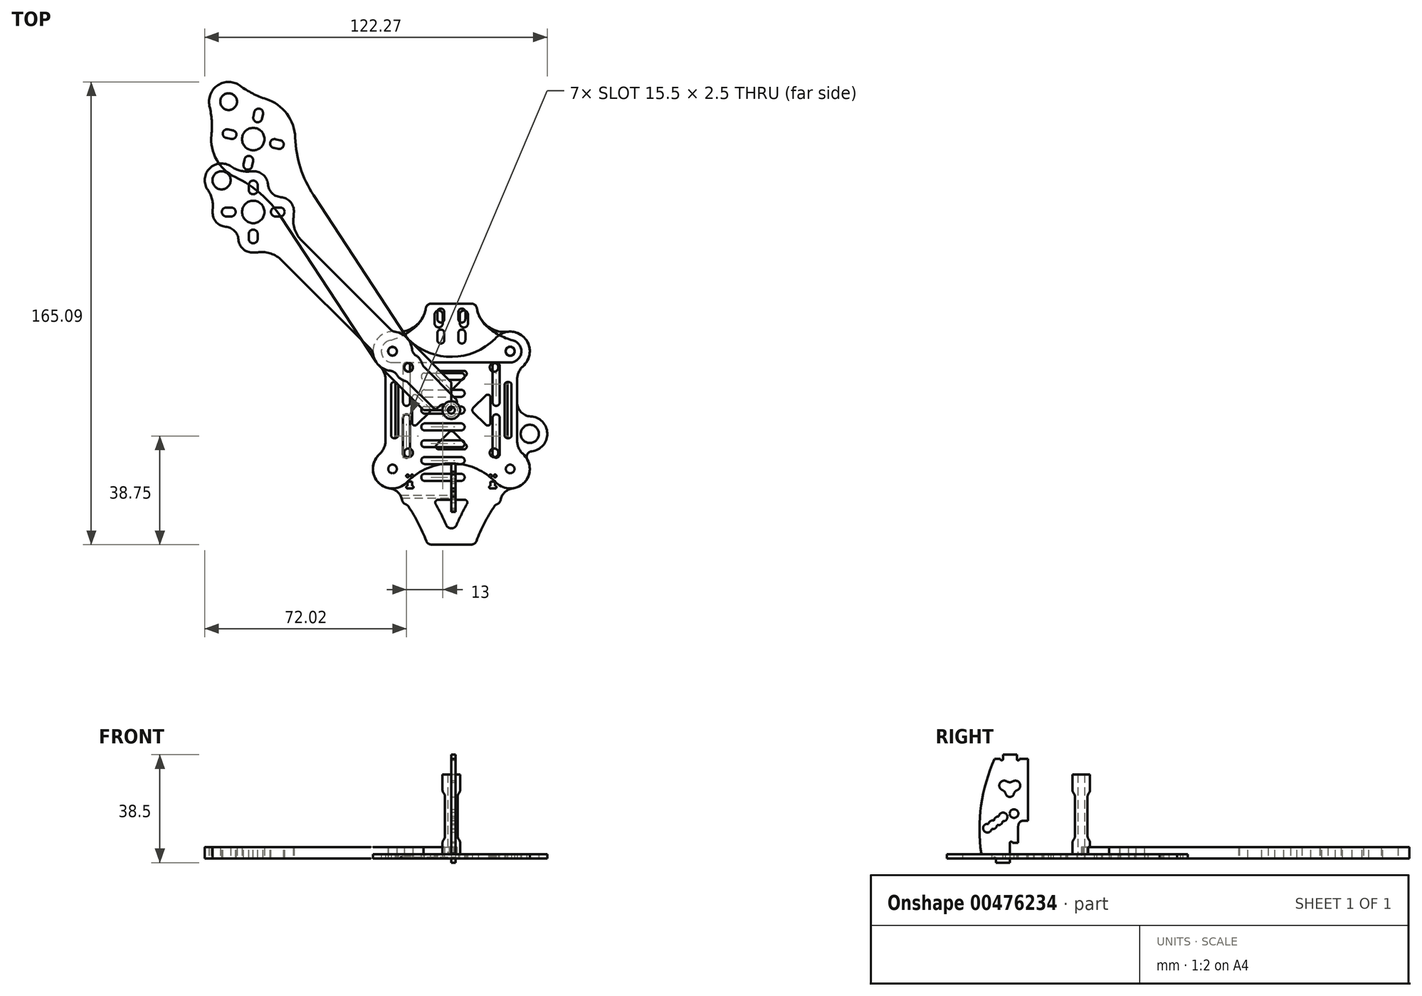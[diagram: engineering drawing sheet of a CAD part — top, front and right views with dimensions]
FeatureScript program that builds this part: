
annotation { "Feature Type Name" : "Feature", "Feature Type Description" : "" }
export const myFeature = defineFeature(function(context is Context, id is Id, definition is map)
    precondition{}
    {
        {
            var Q0;
            Q0=qCreatedBy(makeId("Top.planeOp"),FACE);
            var sketch = newSketch(context, id + "F0", { "sketchPlane" : qUnion([Q0])});
            skCircle(sketch, "E0", {"center": v(-15.25, 15.25) * mm, "radius": 1.55 * mm});
            skCircle(sketch, "E1", {"center": v(15.25, 15.25) * mm, "radius": 1.55 * mm});
            skCircle(sketch, "E2", {"center": v(15.25, -15.25) * mm, "radius": 1.55 * mm});
            skCircle(sketch, "E3", {"center": v(-15.25, -15.25) * mm, "radius": 1.55 * mm});
            skCircle(sketch, "E4", {"center": v(-21, 21) * mm, "radius": 1.55 * mm});
            skCircle(sketch, "E5.MirrorC", {"center": v(21, 21) * mm, "radius": 1.55 * mm});
            skCircle(sketch, "E6.MirrorC", {"center": v(-21, -21) * mm, "radius": 1.55 * mm});
            skCircle(sketch, "E7.MirrorC", {"center": v(21, -21) * mm, "radius": 1.55 * mm});
            skArc(sketch, "E8", {"start": v(-16.05, 25.95) * mm, "mid": v(-25.95, 25.95) * mm, "end": v(-25.95, 16.05) * mm});
            skLineSegment(sketch, "E9", {"start": v(-19, 9) * mm, "end": v(-19, -9) * mm});
            skLineSegment(sketch, "E10", {"start": v(-16.05, 25.95) * mm, "end": v(-15.56, 25.46) * mm});
            skLineSegment(sketch, "E11", {"start": v(-25.95, 16.05) * mm, "end": v(-23.5, 13.6) * mm});
            skLineSegment(sketch, "E12.MirrorCS", {"start": v(-25.95, -16.05) * mm, "end": v(-23.5, -13.6) * mm});
            skArc(sketch, "E13.MirrorCS", {"start": v(-16.05, -25.95) * mm, "mid": v(-25.95, -25.95) * mm, "end": v(-25.95, -16.05) * mm});
            skLineSegment(sketch, "E14.MirrorCS", {"start": v(-16.05, -25.95) * mm, "end": v(-15.56, -25.46) * mm});
            skLineSegment(sketch, "E15.MirrorCS", {"start": v(16.05, 25.95) * mm, "end": v(15.56, 25.46) * mm});
            skArc(sketch, "E16.MirrorCS", {"start": v(16.05, 25.95) * mm, "mid": v(25.95, 25.95) * mm, "end": v(25.95, 16.05) * mm});
            skLineSegment(sketch, "E17.MirrorCS", {"start": v(25.95, 16.05) * mm, "end": v(23.5, 13.6) * mm});
            skLineSegment(sketch, "E18.MirrorCS", {"start": v(25.95, -16.05) * mm, "end": v(23.5, -13.6) * mm});
            skArc(sketch, "E19.MirrorCS", {"start": v(16.05, -25.95) * mm, "mid": v(25.95, -25.95) * mm, "end": v(25.95, -16.05) * mm});
            skLineSegment(sketch, "E20.MirrorCS", {"start": v(16.05, -25.95) * mm, "end": v(15.56, -25.46) * mm});
            skPoint(sketch, "E21.visualSharp", {"position": v(0, 9.9) * mm});
            skPoint(sketch, "E22.visualSharp", {"position": v(0, -9.9) * mm});
            skArc(sketch, "E22.filletArc", {"start": v(15.56, -25.46) * mm, "mid": v(0, -19.01) * mm, "end": v(-15.56, -25.46) * mm});
            skLineSegment(sketch, "E23", {"start": v(-21, 21) * mm, "end": v(0, 0) * mm, "construction": true});
            skArc(sketch, "E24.filletArc", {"start": v(-15.56, 25.46) * mm, "mid": v(0, 19.01) * mm, "end": v(15.56, 25.46) * mm});
            skLineSegment(sketch, "E25", {"start": v(-21.5, 9) * mm, "end": v(-21.5, -9) * mm});
            skLineSegment(sketch, "E26", {"start": v(-23.5, 13.6) * mm, "end": v(-23.5, -13.6) * mm});
            skLineSegment(sketch, "E27", {"start": v(-20.5, 10) * mm, "end": v(-20, 10) * mm});
            skLineSegment(sketch, "E28", {"start": v(-20.5, -10) * mm, "end": v(-20, -10) * mm});
            skPoint(sketch, "E29.visualSharp", {"position": v(-21.5, 10) * mm});
            skArc(sketch, "E29.filletArc", {"start": v(-20.5, 10) * mm, "mid": v(-21.2, 9.7) * mm, "end": v(-21.5, 9) * mm});
            skPoint(sketch, "E30.visualSharp", {"position": v(-19, 10) * mm});
            skArc(sketch, "E30.filletArc", {"start": v(-19, 9) * mm, "mid": v(-19.3, 9.7) * mm, "end": v(-20, 10) * mm});
            skPoint(sketch, "E31.visualSharp", {"position": v(-21.5, -10) * mm});
            skArc(sketch, "E31.filletArc", {"start": v(-21.5, -9) * mm, "mid": v(-21.2, -9.7) * mm, "end": v(-20.5, -10) * mm});
            skPoint(sketch, "E32.visualSharp", {"position": v(-19, -10) * mm});
            skArc(sketch, "E32.filletArc", {"start": v(-20, -10) * mm, "mid": v(-19.3, -9.7) * mm, "end": v(-19, -9) * mm});
            skLineSegment(sketch, "E33.MirrorCS", {"start": v(20.5, -10) * mm, "end": v(20, -10) * mm});
            skLineSegment(sketch, "E34.MirrorCS", {"start": v(20.5, 10) * mm, "end": v(20, 10) * mm});
            skArc(sketch, "E35.MirrorCS", {"start": v(20, -10) * mm, "mid": v(19.3, -9.7) * mm, "end": v(19, -9) * mm});
            skArc(sketch, "E36.MirrorCS", {"start": v(20.5, 10) * mm, "mid": v(21.2, 9.7) * mm, "end": v(21.5, 9) * mm});
            skArc(sketch, "E37.MirrorCS", {"start": v(21.5, -9) * mm, "mid": v(21.2, -9.7) * mm, "end": v(20.5, -10) * mm});
            skArc(sketch, "E38.MirrorCS", {"start": v(19, 9) * mm, "mid": v(19.3, 9.7) * mm, "end": v(20, 10) * mm});
            skPoint(sketch, "E39.MirrorP", {"position": v(19, -10) * mm});
            skLineSegment(sketch, "E40.MirrorCS", {"start": v(23.5, 13.6) * mm, "end": v(23.5, -13.6) * mm});
            skLineSegment(sketch, "E41.MirrorCS", {"start": v(19, 9) * mm, "end": v(19, -9) * mm});
            skPoint(sketch, "E42.MirrorP", {"position": v(21.5, -10) * mm});
            skPoint(sketch, "E43.MirrorP", {"position": v(21.5, 10) * mm});
            skPoint(sketch, "E44.MirrorP", {"position": v(19, 10) * mm});
            skLineSegment(sketch, "E45.MirrorCS", {"start": v(21.5, 9) * mm, "end": v(21.5, -9) * mm});
            skLineSegment(sketch, "E46", {"start": v(0, 0) * mm, "end": v(21, -21) * mm, "construction": true});
            skLineSegment(sketch, "E47", {"start": v(21, 21) * mm, "end": v(-21, -21) * mm, "construction": true});
            skLineSegment(sketch, "E48.0", {"start": v(0.7, -7.78) * mm, "end": v(5.22, -12.3) * mm});
            skLineSegment(sketch, "E48.1", {"start": v(-12.3, 5.22) * mm, "end": v(-7.78, 0.7) * mm});
            skLineSegment(sketch, "E49.0", {"start": v(-5.22, 12.3) * mm, "end": v(-0.7, 7.78) * mm});
            skLineSegment(sketch, "E50.0", {"start": v(7.78, -0.7) * mm, "end": v(12.3, -5.22) * mm});
            skLineSegment(sketch, "E51.MirrorCS", {"start": v(5.22, 12.3) * mm, "end": v(0.7, 7.78) * mm});
            skLineSegment(sketch, "E52.MirrorCS", {"start": v(12.3, 5.22) * mm, "end": v(7.78, 0.7) * mm});
            skLineSegment(sketch, "E53.MirrorCS", {"start": v(-0.7, -7.78) * mm, "end": v(-5.22, -12.3) * mm});
            skLineSegment(sketch, "E54.MirrorCS", {"start": v(-7.78, -0.7) * mm, "end": v(-12.3, -5.22) * mm});
            skPoint(sketch, "E55.orphan", {"position": v(-3.54, -3.54) * mm});
            skPoint(sketch, "E56.orphan", {"position": v(3.54, -3.54) * mm});
            skLineSegment(sketch, "E57", {"start": v(-4.51, 14) * mm, "end": v(4.51, 14) * mm});
            skLineSegment(sketch, "E58", {"start": v(-14, 4.51) * mm, "end": v(-14, -4.51) * mm});
            skLineSegment(sketch, "E59", {"start": v(-4.51, -14) * mm, "end": v(4.51, -14) * mm});
            skLineSegment(sketch, "E60", {"start": v(14, -4.51) * mm, "end": v(14, 4.51) * mm});
            skPoint(sketch, "E61.visualSharp", {"position": v(-14, 6.93) * mm});
            skArc(sketch, "E61.filletArc", {"start": v(-12.3, 5.22) * mm, "mid": v(-13.38, 5.44) * mm, "end": v(-14, 4.51) * mm});
            skPoint(sketch, "E62.visualSharp", {"position": v(-14, -6.93) * mm});
            skArc(sketch, "E62.filletArc", {"start": v(-14, -4.51) * mm, "mid": v(-13.38, -5.44) * mm, "end": v(-12.3, -5.22) * mm});
            skPoint(sketch, "E63.visualSharp", {"position": v(-7.07, 0) * mm});
            skArc(sketch, "E63.filletArc", {"start": v(-7.78, -0.7) * mm, "mid": v(-7.49, 0) * mm, "end": v(-7.78, 0.7) * mm});
            skPoint(sketch, "E64.visualSharp", {"position": v(0, -7.07) * mm});
            skArc(sketch, "E64.filletArc", {"start": v(0.7, -7.78) * mm, "mid": v(0, -7.49) * mm, "end": v(-0.7, -7.78) * mm});
            skPoint(sketch, "E65.visualSharp", {"position": v(-6.93, -14) * mm});
            skArc(sketch, "E65.filletArc", {"start": v(-5.22, -12.3) * mm, "mid": v(-5.44, -13.38) * mm, "end": v(-4.51, -14) * mm});
            skPoint(sketch, "E66.visualSharp", {"position": v(6.93, -14) * mm});
            skArc(sketch, "E66.filletArc", {"start": v(4.51, -14) * mm, "mid": v(5.44, -13.38) * mm, "end": v(5.22, -12.3) * mm});
            skPoint(sketch, "E67.visualSharp", {"position": v(14, -6.93) * mm});
            skArc(sketch, "E67.filletArc", {"start": v(12.3, -5.22) * mm, "mid": v(13.38, -5.44) * mm, "end": v(14, -4.51) * mm});
            skPoint(sketch, "E68.visualSharp", {"position": v(14, 6.93) * mm});
            skArc(sketch, "E68.filletArc", {"start": v(14, 4.51) * mm, "mid": v(13.38, 5.44) * mm, "end": v(12.3, 5.22) * mm});
            skPoint(sketch, "E69.visualSharp", {"position": v(7.07, 0) * mm});
            skArc(sketch, "E69.filletArc", {"start": v(7.78, 0.7) * mm, "mid": v(7.49, 0) * mm, "end": v(7.78, -0.7) * mm});
            skPoint(sketch, "E70.visualSharp", {"position": v(0, 7.07) * mm});
            skArc(sketch, "E70.filletArc", {"start": v(-0.7, 7.78) * mm, "mid": v(0, 7.49) * mm, "end": v(0.7, 7.78) * mm});
            skPoint(sketch, "E71.visualSharp", {"position": v(-6.93, 14) * mm});
            skArc(sketch, "E71.filletArc", {"start": v(-4.51, 14) * mm, "mid": v(-5.44, 13.38) * mm, "end": v(-5.22, 12.3) * mm});
            skPoint(sketch, "E72.visualSharp", {"position": v(6.93, 14) * mm});
            skArc(sketch, "E72.filletArc", {"start": v(5.22, 12.3) * mm, "mid": v(5.44, 13.38) * mm, "end": v(4.51, 14) * mm});
            skSolve(sketch);
        }
        {
            var Q0;
            Q0=makeQuery(id+"F0.imprint","IMPRINT",FACE,{"disambiguationData":[TD([[makeQuery(id+"F0.imprint","IMPRINT",EDGE,{"derivedFrom":sQuery(id+"F0.wireOp",EDGE,"E0")}),-1.0]])]});
            extrude(context, id + "F1", {"entities" : qUnion([Q0]), "depth" : 1.5 * mm});
        }
        {
            var Q0;
            Q0=qCreatedBy(makeId("Top.planeOp"),FACE);
            var sketch = newSketch(context, id + "F2", { "sketchPlane" : qUnion([Q0])});
            skCircle(sketch, "E73", {"center": v(-15.25, 15.25) * mm, "radius": 1.55 * mm});
            skCircle(sketch, "E74", {"center": v(-21, 21) * mm, "radius": 1.55 * mm});
            skArc(sketch, "E75", {"start": v(-20.18, 27.95) * mm, "mid": v(-27.3, 24.06) * mm, "end": v(-25.95, 16.05) * mm});
            skLineSegment(sketch, "E76", {"start": v(-19, 9) * mm, "end": v(-19, 0) * mm});
            skPoint(sketch, "E77.visualSharp", {"position": v(-19, 10) * mm});
            skArc(sketch, "E77.filletArc", {"start": v(-19, 9) * mm, "mid": v(-19.26, 9.67) * mm, "end": v(-19.9, 10) * mm});
            skLineSegment(sketch, "E78", {"start": v(0, 38) * mm, "end": v(0, -38) * mm, "construction": true});
            skArc(sketch, "E79.MirrorCS", {"start": v(19, 9) * mm, "mid": v(19.26, 9.67) * mm, "end": v(19.9, 10) * mm});
            skLineSegment(sketch, "E80.MirrorCS", {"start": v(19, 9) * mm, "end": v(19, 0) * mm});
            skArc(sketch, "E81.MirrorCS", {"start": v(20.18, 27.95) * mm, "mid": v(27.3, 24.06) * mm, "end": v(25.95, 16.05) * mm});
            skCircle(sketch, "E82.MirrorC", {"center": v(21, 21) * mm, "radius": 1.55 * mm});
            skCircle(sketch, "E83.MirrorC", {"center": v(15.25, 15.25) * mm, "radius": 1.55 * mm});
            skPoint(sketch, "E84.MirrorP", {"position": v(19, 10) * mm});
            skPoint(sketch, "E85.MirrorP", {"position": v(19, -10) * mm});
            skArc(sketch, "E86.MirrorCS", {"start": v(19, -9) * mm, "mid": v(19.26, -9.67) * mm, "end": v(19.9, -10) * mm});
            skLineSegment(sketch, "E87.MirrorCS", {"start": v(19, -9) * mm, "end": v(19, 0) * mm});
            skArc(sketch, "E88.MirrorCS", {"start": v(-19, -9) * mm, "mid": v(-19.26, -9.67) * mm, "end": v(-19.9, -10) * mm});
            skLineSegment(sketch, "E89.MirrorCS", {"start": v(-19, -9) * mm, "end": v(-19, 0) * mm});
            skPoint(sketch, "E90.MirrorP", {"position": v(-19, -10) * mm});
            skCircle(sketch, "E91.MirrorC", {"center": v(-15.25, -15.25) * mm, "radius": 1.55 * mm});
            skCircle(sketch, "E92.MirrorC", {"center": v(-21, -21) * mm, "radius": 1.55 * mm});
            skArc(sketch, "E93.MirrorCS", {"start": v(-22.14, -27.9) * mm, "mid": v(-27.66, -23.14) * mm, "end": v(-25.95, -16.05) * mm});
            skCircle(sketch, "E94.MirrorC", {"center": v(21, -21) * mm, "radius": 1.55 * mm});
            skCircle(sketch, "E95.MirrorC", {"center": v(15.25, -15.25) * mm, "radius": 1.55 * mm});
            skArc(sketch, "E96.MirrorCS", {"start": v(22.14, -27.9) * mm, "mid": v(27.66, -23.14) * mm, "end": v(25.95, -16.05) * mm});
            skArc(sketch, "E97.MirrorCS", {"start": v(22.14, -27.9) * mm, "mid": v(21.69, -28) * mm, "end": v(21.24, -28.1) * mm});
            skArc(sketch, "E98.MirrorCS", {"start": v(-22.14, -27.9) * mm, "mid": v(-21.69, -28) * mm, "end": v(-21.24, -28.1) * mm});
            skLineSegment(sketch, "E99.bottom", {"start": v(-15.6, -25.5) * mm, "end": v(-14, -25.5) * mm});
            skLineSegment(sketch, "E99.top", {"start": v(-15.6, -30.5) * mm, "end": v(-14, -30.5) * mm});
            skLineSegment(sketch, "E99.left", {"start": v(-15.6, -25.5) * mm, "end": v(-15.6, -30.5) * mm});
            skLineSegment(sketch, "E99.right", {"start": v(-14, -25.5) * mm, "end": v(-14, -30.5) * mm});
            skLineSegment(sketch, "E100.MirrorCS", {"start": v(15.6, -25.5) * mm, "end": v(14, -25.5) * mm});
            skLineSegment(sketch, "E101.MirrorCS", {"start": v(15.6, -25.5) * mm, "end": v(15.6, -30.5) * mm});
            skLineSegment(sketch, "E102.MirrorCS", {"start": v(14, -25.5) * mm, "end": v(14, -30.5) * mm});
            skLineSegment(sketch, "E103.MirrorCS", {"start": v(15.6, -30.5) * mm, "end": v(14, -30.5) * mm});
            skLineSegment(sketch, "E104", {"start": v(-25.95, -16.05) * mm, "end": v(-25.95, -16.05) * mm});
            skLineSegment(sketch, "E105", {"start": v(-21, -21) * mm, "end": v(0, 0) * mm, "construction": true});
            skLineSegment(sketch, "E106", {"start": v(-17.5, -32.94) * mm, "end": v(-17.5, -33.5) * mm});
            skLineSegment(sketch, "E107", {"start": v(-17.5, -33.5) * mm, "end": v(-16.97, -33.5) * mm});
            skLineSegment(sketch, "E108.MirrorCS", {"start": v(17.5, -32.94) * mm, "end": v(17.5, -33.5) * mm});
            skLineSegment(sketch, "E109.MirrorCS", {"start": v(17.5, -33.5) * mm, "end": v(16.97, -33.5) * mm});
            skArc(sketch, "E110.filletArc", {"start": v(-17.5, -32.94) * mm, "mid": v(-18.54, -29.88) * mm, "end": v(-21.24, -28.1) * mm});
            skArc(sketch, "E111.filletArc", {"start": v(21.24, -28.1) * mm, "mid": v(18.54, -29.88) * mm, "end": v(17.5, -32.94) * mm});
            skLineSegment(sketch, "E112", {"start": v(-25.95, 16.05) * mm, "end": v(-19.9, 10) * mm});
            skLineSegment(sketch, "E113", {"start": v(0, 0) * mm, "end": v(-15.25, 15.25) * mm, "construction": true});
            skLineSegment(sketch, "E114.MirrorCS", {"start": v(-25.95, -16.05) * mm, "end": v(-19.9, -10) * mm});
            skLineSegment(sketch, "E115.MirrorCS", {"start": v(25.95, 16.05) * mm, "end": v(19.9, 10) * mm});
            skLineSegment(sketch, "E116.MirrorCS", {"start": v(25.95, -16.05) * mm, "end": v(19.9, -10) * mm});
            skLineSegment(sketch, "E117", {"start": v(-21, -21) * mm, "end": v(-70.71, -70.71) * mm, "construction": true});
            skCircle(sketch, "E118", {"center": v(-70.71, -70.71) * mm, "radius": 64.25 * mm, "construction": true});
            skArc(sketch, "E119", {"start": v(-8.47, -48) * mm, "mid": v(-11.5, -41) * mm, "end": v(-15.3, -34.4) * mm});
            skLineSegment(sketch, "E120", {"start": v(-8.47, -48) * mm, "end": v(0, -48) * mm});
            skArc(sketch, "E121.MirrorCS", {"start": v(8.47, -48) * mm, "mid": v(11.5, -41) * mm, "end": v(15.3, -34.4) * mm});
            skLineSegment(sketch, "E122.MirrorCS", {"start": v(8.47, -48) * mm, "end": v(0, -48) * mm});
            skArc(sketch, "E123", {"start": v(-20.18, 27.95) * mm, "mid": v(-12.97, 29.9) * mm, "end": v(-9.12, 36.31) * mm});
            skArc(sketch, "E124.MirrorCS", {"start": v(20.18, 27.95) * mm, "mid": v(12.97, 29.9) * mm, "end": v(9.12, 36.31) * mm});
            skPoint(sketch, "E125.visualSharp", {"position": v(-15.9, -33.5) * mm});
            skArc(sketch, "E125.filletArc", {"start": v(-15.3, -34.4) * mm, "mid": v(-16.02, -33.74) * mm, "end": v(-16.97, -33.5) * mm});
            skPoint(sketch, "E126.visualSharp", {"position": v(15.9, -33.5) * mm});
            skArc(sketch, "E126.filletArc", {"start": v(16.97, -33.5) * mm, "mid": v(16.02, -33.74) * mm, "end": v(15.3, -34.4) * mm});
            skLineSegment(sketch, "E127", {"start": v(-7.15, 38) * mm, "end": v(7.15, 38) * mm});
            skPoint(sketch, "E128.orphan", {"position": v(-8.47, 48) * mm});
            skPoint(sketch, "E129.orphan", {"position": v(8.47, 48) * mm});
            skPoint(sketch, "E130.visualSharp", {"position": v(-9, 38) * mm});
            skArc(sketch, "E130.filletArc", {"start": v(-7.15, 38) * mm, "mid": v(-8.45, 37.52) * mm, "end": v(-9.12, 36.31) * mm});
            skPoint(sketch, "E131.visualSharp", {"position": v(9, 38) * mm});
            skArc(sketch, "E131.filletArc", {"start": v(9.12, 36.31) * mm, "mid": v(8.45, 37.52) * mm, "end": v(7.15, 38) * mm});
            skCircle(sketch, "E132", {"center": v(0, 0) * mm, "radius": 5 * mm});
            skSolve(sketch);
        }
        {
            var Q0;
            Q0=makeQuery(id+"F2.imprint","IMPRINT",FACE,{"disambiguationData":[TD([[makeQuery(id+"F2.imprint","IMPRINT",EDGE,{"derivedFrom":sQuery(id+"F2.wireOp",EDGE,"E73")}),-1.0]])]});
            extrude(context, id + "F3", {"entities" : qUnion([Q0]), "depth" : 1.5 * mm});
        }
        {
            var Q0;
            Q0=makeQuery(id+"F3.opExtrude","CAP_FACE",FACE,{"disambiguationData":[OSD([sQuery(id+"F2.wireOp",EDGE,"E73"),sQuery(id+"F2.wireOp",EDGE,"jFPTTxz4-jLXj-DDCv-FC09-USVAbM95QFUD"),sQuery(id+"F2.wireOp",EDGE,"E74"),sQuery(id+"F2.wireOp",EDGE,"E75"),sQuery(id+"F2.wireOp",EDGE,"E76"),sQuery(id+"F2.wireOp",EDGE,"OV2Wl9yg-sUyD-2Hj2-rkXj-MTIEYF9VZsJK"),sQuery(id+"F2.wireOp",EDGE,"91e39d24-f0d0-409c-99ef-685c742f9300.filletArc"),sQuery(id+"F2.wireOp",EDGE,"E77.filletArc"),sQuery(id+"F2.wireOp",EDGE,"2RSG9yHZ-WQqx-c2xK-pqDh-UdEIjaxC7IlA"),sQuery(id+"F2.wireOp",EDGE,"4rgxPuH5-7xbP-ZsFa-2w6e-7YXQlRziYjOP"),sQuery(id+"F2.wireOp",EDGE,"aAb2sQRX-3QeW-SLoE-m21K-AacbavdIfjy6"),sQuery(id+"F2.wireOp",EDGE,"7c283ec5-88dc-4330-9acd-45fa73696fd10.MirrorCS"),sQuery(id+"F2.wireOp",EDGE,"E79.MirrorCS"),sQuery(id+"F2.wireOp",EDGE,"E80.MirrorCS"),sQuery(id+"F2.wireOp",EDGE,"E81.MirrorCS"),sQuery(id+"F2.wireOp",EDGE,"E82.MirrorC"),sQuery(id+"F2.wireOp",EDGE,"E792.MirrorC"),sQuery(id+"F2.wireOp",EDGE,"E83.MirrorC"),sQuery(id+"F2.wireOp",EDGE,"E794.MirrorCS"),sQuery(id+"F2.wireOp",EDGE,"E796.MirrorCS"),sQuery(id+"F2.wireOp",EDGE,"77becaeb-8b8b-4dc1-b250-45090536f0a20.MirrorCS"),sQuery(id+"F2.wireOp",EDGE,"26ce58a3-4cb5-4f15-a1e7-5b8d20efb5c40.MirrorCS"),sQuery(id+"F2.wireOp",EDGE,"E86.MirrorCS"),sQuery(id+"F2.wireOp",EDGE,"9822711c-84ae-4c2d-bbd4-b3a60979fe174.MirrorCS"),sQuery(id+"F2.wireOp",EDGE,"E87.MirrorCS"),sQuery(id+"F2.wireOp",EDGE,"9822711c-84ae-4c2d-bbd4-b3a60979fe176.MirrorCS"),sQuery(id+"F2.wireOp",EDGE,"E88.MirrorCS"),sQuery(id+"F2.wireOp",EDGE,"4a2114cf-ddcc-4bd1-b273-f588f7a722dc1.MirrorCS"),sQuery(id+"F2.wireOp",EDGE,"4a2114cf-ddcc-4bd1-b273-f588f7a722dc2.MirrorCS"),sQuery(id+"F2.wireOp",EDGE,"E89.MirrorCS"),sQuery(id+"F2.wireOp",EDGE,"E91.MirrorC"),sQuery(id+"F2.wireOp",EDGE,"E92.MirrorC"),sQuery(id+"F2.wireOp",EDGE,"E93.MirrorCS"),sQuery(id+"F2.wireOp",EDGE,"E94.MirrorC"),sQuery(id+"F2.wireOp",EDGE,"E95.MirrorC"),sQuery(id+"F2.wireOp",EDGE,"5bfa031d-9f72-4db7-bc0c-70e661b370ed0.MirrorC"),sQuery(id+"F2.wireOp",EDGE,"6425a8bc-ce2c-4a8b-8028-989707d169630.MirrorC"),sQuery(id+"F2.wireOp",EDGE,"E96.MirrorCS"),sQuery(id+"F2.wireOp",EDGE,"E97.MirrorCS"),sQuery(id+"F2.wireOp",EDGE,"32760b4d-dda8-4da2-a85d-3a466e5e60c60.MirrorCS"),sQuery(id+"F2.wireOp",EDGE,"3608dae1-eb2e-4dc6-816e-64e42f027ba40.MirrorCS"),sQuery(id+"F2.wireOp",EDGE,"E98.MirrorCS"),sQuery(id+"F2.wireOp",EDGE,"c6e026e1-fe79-4e24-8aee-e9c260e0377b0.MirrorCS"),sQuery(id+"F2.wireOp",EDGE,"681415bc-d1ca-493e-a100-2ccd6f0434aa0.MirrorCS"),sQuery(id+"F2.wireOp",EDGE,"E99.bottom"),sQuery(id+"F2.wireOp",EDGE,"E99.top"),sQuery(id+"F2.wireOp",EDGE,"E99.left"),sQuery(id+"F2.wireOp",EDGE,"E99.right"),sQuery(id+"F2.wireOp",EDGE,"E100.MirrorCS"),sQuery(id+"F2.wireOp",EDGE,"E101.MirrorCS"),sQuery(id+"F2.wireOp",EDGE,"E102.MirrorCS"),sQuery(id+"F2.wireOp",EDGE,"E103.MirrorCS"),sQuery(id+"F2.wireOp",EDGE,"VBkXurKH-HzS8-dzkn-LxKA-4I1jdE3c4Em0"),sQuery(id+"F2.wireOp",EDGE,"b7184078-a67c-4706-b7f2-105a01179b9c.filletArc"),sQuery(id+"F2.wireOp",EDGE,"b7237c02-60dc-40f2-a213-8a94564c20be0.MirrorCS"),sQuery(id+"F2.wireOp",EDGE,"bdf4f6a4-df0c-4300-a64c-7dace4eac6310.MirrorCS"),sQuery(id+"F2.wireOp",EDGE,"ee7ddf88-5d4a-4064-9a04-f45d6847952f0.MirrorCS"),sQuery(id+"F2.wireOp",EDGE,"de45aa2e-6ca1-40a2-bc78-a00ece19e9440.MirrorCS"),sQuery(id+"F2.wireOp",EDGE,"1337a31e-3a8f-42fa-aa43-79b785e411150.MirrorCS"),sQuery(id+"F2.wireOp",EDGE,"daa37f43-5825-406c-9ff9-18d668761be80.MirrorCS")])],"isStart":true});
            var sketch = newSketch(context, id + "F4", { "sketchPlane" : qUnion([Q0])});
            skCircle(sketch, "E133", {"center": v(-15.6, 30) * mm, "radius": 0.5 * mm});
            skCircle(sketch, "E134", {"center": v(-14, 30) * mm, "radius": 0.5 * mm});
            skCircle(sketch, "E135", {"center": v(-15.6, 26) * mm, "radius": 0.5 * mm});
            skCircle(sketch, "E136", {"center": v(-14, 26) * mm, "radius": 0.5 * mm});
            skCircle(sketch, "E137.MirrorC", {"center": v(14, 26) * mm, "radius": 0.5 * mm});
            skCircle(sketch, "E138.MirrorC", {"center": v(15.6, 30) * mm, "radius": 0.5 * mm});
            skCircle(sketch, "E139.MirrorC", {"center": v(14, 30) * mm, "radius": 0.5 * mm});
            skCircle(sketch, "E140.MirrorC", {"center": v(15.6, 26) * mm, "radius": 0.5 * mm});
            skSolve(sketch);
        }
        {
            var Q0;
            Q0=qSketchRegion(id+"F4",true);
            extrude(context, id + "F5", {"entities" : qUnion([Q0]), "operationType" : NewBodyOperationType.REMOVE, "oppositeDirection" : true, "depth" : 25 * mm});
        }
        {
            var Q0;
            Q0=qCreatedBy(makeId("Top.planeOp"),FACE);
            var sketch = newSketch(context, id + "F6", { "sketchPlane" : qUnion([Q0])});
            skCircle(sketch, "E141", {"center": v(-15.25, 15.25) * mm, "radius": 1.52 * mm});
            skCircle(sketch, "E142", {"center": v(-21, 21) * mm, "radius": 1.52 * mm});
            skLineSegment(sketch, "E143", {"start": v(0, 0) * mm, "end": v(-70.71, 70.71) * mm, "construction": true});
            skLineSegment(sketch, "E144", {"start": v(-21.7, 28.78) * mm, "end": v(-53.48, 60.55) * mm});
            skArc(sketch, "E145", {"start": v(-85.16, 71.97) * mm, "mid": v(-84.99, 68.17) * mm, "end": v(-83.84, 64.55) * mm});
            skArc(sketch, "E146", {"start": v(-78.58, 86.93) * mm, "mid": v(-86.27, 86.27) * mm, "end": v(-86.93, 78.58) * mm});
            skCircle(sketch, "E147", {"center": v(-82.02, 82.02) * mm, "radius": 3.25 * mm});
            skLineSegment(sketch, "E148", {"start": v(-70.71, 70.71) * mm, "end": v(-82.02, 82.02) * mm, "construction": true});
            skPoint(sketch, "E149.visualSharp", {"position": v(-76.38, 84.06) * mm});
            skArc(sketch, "E149.filletArc", {"start": v(-78.58, 86.93) * mm, "mid": v(-75.43, 85.46) * mm, "end": v(-71.97, 85.16) * mm});
            skPoint(sketch, "E150.visualSharp", {"position": v(-84.06, 76.38) * mm});
            skArc(sketch, "E150.filletArc", {"start": v(-85.16, 71.97) * mm, "mid": v(-85.46, 75.43) * mm, "end": v(-86.93, 78.58) * mm});
            skCircle(sketch, "E151", {"center": v(-70.71, 70.71) * mm, "radius": 64.25 * mm, "construction": true});
            skArc(sketch, "E152.trimOffspring", {"start": v(-56.33, 68.88) * mm, "mid": v(-56.39, 72.97) * mm, "end": v(-57.58, 76.87) * mm});
            skPoint(sketch, "E153.visualSharp", {"position": v(-57.55, 64.62) * mm});
            skArc(sketch, "E153.filletArc", {"start": v(-56.33, 68.88) * mm, "mid": v(-55.87, 64.38) * mm, "end": v(-53.48, 60.55) * mm});
            skArc(sketch, "E154.filletArc", {"start": v(-60.55, 53.48) * mm, "mid": v(-64.38, 55.87) * mm, "end": v(-68.88, 56.33) * mm});
            skCircle(sketch, "E155", {"center": v(-70.71, 70.71) * mm, "radius": 4 * mm});
            skArc(sketch, "E156.trimOffspring", {"start": v(-10.44, 16.63) * mm, "mid": v(-11.27, 18.27) * mm, "end": v(-12.63, 19.5) * mm});
            skLineSegment(sketch, "E157", {"start": v(-5.66, 0) * mm, "end": v(-15.34, 9.68) * mm});
            skLineSegment(sketch, "E158", {"start": v(-9.68, 15.34) * mm, "end": v(0, 5.66) * mm});
            skArc(sketch, "E159.trimOffspring", {"start": v(-10.44, 16.63) * mm, "mid": v(-11.78, 18.85) * mm, "end": v(-14.06, 20.1) * mm});
            skPoint(sketch, "E160.orphan", {"position": v(0, 7.07) * mm});
            skPoint(sketch, "E161.visualSharp", {"position": v(-15.96, 10.3) * mm});
            skArc(sketch, "E161.filletArc", {"start": v(-15.34, 9.68) * mm, "mid": v(-15.94, 10.15) * mm, "end": v(-16.63, 10.44) * mm});
            skPoint(sketch, "E162.visualSharp", {"position": v(-10.3, 15.96) * mm});
            skArc(sketch, "E162.filletArc", {"start": v(-10.44, 16.63) * mm, "mid": v(-10.15, 15.94) * mm, "end": v(-9.68, 15.34) * mm});
            skArc(sketch, "E163", {"start": v(-1.41, 1.41) * mm, "mid": v(1.41, 1.41) * mm, "end": v(1.41, 4.24) * mm});
            skArc(sketch, "E164", {"start": v(-1.41, 1.41) * mm, "mid": v(-2.83, 2) * mm, "end": v(-4.24, 1.41) * mm});
            skLineSegment(sketch, "E165", {"start": v(0, 5.66) * mm, "end": v(1.41, 4.24) * mm});
            skLineSegment(sketch, "E166", {"start": v(-4.24, 1.41) * mm, "end": v(-5.66, 0) * mm});
            skArc(sketch, "E167", {"start": v(-14.04, 21.74) * mm, "mid": v(-15.96, 25.86) * mm, "end": v(-20.01, 27.93) * mm});
            skLineSegment(sketch, "E168.trimOffspring", {"start": v(-28.78, 21.7) * mm, "end": v(-60.55, 53.48) * mm});
            skArc(sketch, "E169.trimOffspring", {"start": v(-19.5, 12.63) * mm, "mid": v(-18.27, 11.27) * mm, "end": v(-16.63, 10.44) * mm});
            skArc(sketch, "E170.trimOffspring", {"start": v(-27.93, 20.01) * mm, "mid": v(-25.86, 15.96) * mm, "end": v(-21.74, 14.04) * mm});
            skPoint(sketch, "E171.visualSharp", {"position": v(-20.1, 14.06) * mm});
            skArc(sketch, "E171.filletArc", {"start": v(-19.5, 12.63) * mm, "mid": v(-20.46, 13.6) * mm, "end": v(-21.74, 14.04) * mm});
            skPoint(sketch, "E172.visualSharp", {"position": v(-14.06, 20.1) * mm});
            skArc(sketch, "E172.filletArc", {"start": v(-14.04, 21.74) * mm, "mid": v(-13.6, 20.46) * mm, "end": v(-12.63, 19.5) * mm});
            skPoint(sketch, "E173.visualSharp", {"position": v(-28, 20.93) * mm});
            skArc(sketch, "E173.filletArc", {"start": v(-27.93, 20.01) * mm, "mid": v(-28.22, 20.93) * mm, "end": v(-28.78, 21.7) * mm});
            skPoint(sketch, "E174.visualSharp", {"position": v(-20.93, 28) * mm});
            skArc(sketch, "E174.filletArc", {"start": v(-21.7, 28.78) * mm, "mid": v(-20.93, 28.22) * mm, "end": v(-20.01, 27.93) * mm});
            skArc(sketch, "E175", {"start": v(-64.55, 83.84) * mm, "mid": v(-64, 77.43) * mm, "end": v(-57.58, 76.87) * mm});
            skArc(sketch, "E176.trimOffspring", {"start": v(-64.55, 83.84) * mm, "mid": v(-68.17, 84.99) * mm, "end": v(-71.97, 85.16) * mm});
            skLineSegment(sketch, "E177", {"start": v(-70.71, 70.71) * mm, "end": v(-60.46, 80.96) * mm, "construction": true});
            skArc(sketch, "E178.MirrorCS", {"start": v(-83.84, 64.55) * mm, "mid": v(-77.43, 64) * mm, "end": v(-76.87, 57.58) * mm});
            skArc(sketch, "E179.trimOffspring", {"start": v(-76.87, 57.58) * mm, "mid": v(-72.97, 56.39) * mm, "end": v(-68.88, 56.33) * mm});
            skSolve(sketch);
        }
        {
            var Q0;
            Q0=qSketchRegion(id+"F6",true);
            extrude(context, id + "F7", {"entities" : qUnion([Q0]), "depth" : 4 * mm});
        }
        {
            var Q0;
            Q0=makeQuery(id+"F7.opExtrude","CAP_FACE",FACE,{"disambiguationData":[OSD([sQuery(id+"F6.wireOp",EDGE,"ELmgnBSW-vcTX-69ba-dwwi-cACzyNvr3Jda"),sQuery(id+"F6.wireOp",EDGE,"E141"),sQuery(id+"F6.wireOp",EDGE,"E142"),sQuery(id+"F6.wireOp",EDGE,"wzC1F6xg-fGIV-3KpO-c9gR-K1YJSPa7NM8s"),sQuery(id+"F6.wireOp",EDGE,"E144"),sQuery(id+"F6.wireOp",EDGE,"FoUFOdND-4TSw-zWgQ-ILiy-lV2VMV41Ndkk"),sQuery(id+"F6.wireOp",EDGE,"gZyNtGtT-cGv0-NfnX-XPpx-gTdD2O9JXBFj"),sQuery(id+"F6.wireOp",EDGE,"AxQfXuDg-QIAQ-o6Jz-UGCb-lciMLiFu8Ysp"),sQuery(id+"F6.wireOp",EDGE,"495c5933-9560-4cef-81c8-4e8a0d039e08.trimOffspring"),sQuery(id+"F6.wireOp",EDGE,"x8G4jeR7-3K2l-pC60-u55W-RZAUUndLqHre"),sQuery(id+"F6.wireOp",EDGE,"JV1SctKD-Vwmc-S0x5-JHBv-4d7ALUXfkLMJ"),sQuery(id+"F6.wireOp",EDGE,"ef546a75-4e02-40f2-ac6e-af8522daafdd.filletArc"),sQuery(id+"F6.wireOp",EDGE,"2512e942-d075-422c-a12b-7db6a64d2190.filletArc"),sQuery(id+"F6.wireOp",EDGE,"E145"),sQuery(id+"F6.wireOp",EDGE,"E146"),sQuery(id+"F6.wireOp",EDGE,"E147"),sQuery(id+"F6.wireOp",EDGE,"E149.filletArc"),sQuery(id+"F6.wireOp",EDGE,"E150.filletArc"),sQuery(id+"F6.wireOp",EDGE,"E152.trimOffspring"),sQuery(id+"F6.wireOp",EDGE,"E153.filletArc"),sQuery(id+"F6.wireOp",EDGE,"E154.filletArc"),sQuery(id+"F6.wireOp",EDGE,"E155")])],"isStart":false});
            var sketch = newSketch(context, id + "F8", { "sketchPlane" : qUnion([Q0])});
            skLineSegment(sketch, "E180", {"start": v(-70.71, 70.71) * mm, "end": v(-62.81, 70.71) * mm, "construction": true});
            skLineSegment(sketch, "E181", {"start": v(-70.71, 70.71) * mm, "end": v(0, 0) * mm, "construction": true});
            skLineSegment(sketch, "E182", {"start": v(-62.81, 70.71) * mm, "end": v(-61.11, 70.71) * mm, "construction": true});
            skArc(sketch, "E183.0.startCap", {"start": v(-62.81, 69.11) * mm, "mid": v(-64.41, 70.71) * mm, "end": v(-62.81, 72.31) * mm});
            skArc(sketch, "E183.0.endCap", {"start": v(-61.11, 72.31) * mm, "mid": v(-59.51, 70.71) * mm, "end": v(-61.11, 69.11) * mm});
            skLineSegment(sketch, "E183.0.left", {"start": v(-62.81, 72.31) * mm, "end": v(-61.11, 72.31) * mm});
            skLineSegment(sketch, "E183.0.right", {"start": v(-62.81, 69.11) * mm, "end": v(-61.11, 69.11) * mm});
            skLineSegment(sketch, "E184.1.0", {"start": v(-72.31, 78.61) * mm, "end": v(-72.31, 80.31) * mm});
            skArc(sketch, "E184.1.1", {"start": v(-69.11, 78.61) * mm, "mid": v(-70.71, 77.01) * mm, "end": v(-72.31, 78.61) * mm});
            skLineSegment(sketch, "E184.1.2", {"start": v(-69.11, 78.61) * mm, "end": v(-69.11, 80.31) * mm});
            skArc(sketch, "E184.1.3", {"start": v(-72.31, 80.31) * mm, "mid": v(-70.71, 81.91) * mm, "end": v(-69.11, 80.31) * mm});
            skLineSegment(sketch, "E184.2.0", {"start": v(-78.61, 69.11) * mm, "end": v(-80.31, 69.11) * mm});
            skArc(sketch, "E184.2.1", {"start": v(-78.61, 72.31) * mm, "mid": v(-77.01, 70.71) * mm, "end": v(-78.61, 69.11) * mm});
            skLineSegment(sketch, "E184.2.2", {"start": v(-78.61, 72.31) * mm, "end": v(-80.31, 72.31) * mm});
            skArc(sketch, "E184.2.3", {"start": v(-80.31, 69.11) * mm, "mid": v(-81.91, 70.71) * mm, "end": v(-80.31, 72.31) * mm});
            skLineSegment(sketch, "E184.3.0", {"start": v(-69.11, 62.81) * mm, "end": v(-69.11, 61.11) * mm});
            skArc(sketch, "E184.3.1", {"start": v(-72.31, 62.81) * mm, "mid": v(-70.71, 64.41) * mm, "end": v(-69.11, 62.81) * mm});
            skLineSegment(sketch, "E184.3.2", {"start": v(-72.31, 62.81) * mm, "end": v(-72.31, 61.11) * mm});
            skArc(sketch, "E184.3.3", {"start": v(-69.11, 61.11) * mm, "mid": v(-70.71, 59.51) * mm, "end": v(-72.31, 61.11) * mm});
            skPoint(sketch, "E184.center", {"position": v(-70.71, 70.71) * mm});
            skSolve(sketch);
        }
        {
            var Q0;
            Q0=qSketchRegion(id+"F8",true);
            extrude(context, id + "F9", {"entities" : qUnion([Q0]), "operationType" : NewBodyOperationType.REMOVE, "oppositeDirection" : true, "depth" : 25 * mm});
        }
        {
            var Q0;
            Q0=qCreatedBy(makeId("Top.planeOp"),FACE);
            var sketch = newSketch(context, id + "F10", { "sketchPlane" : qUnion([Q0])});
            skCircle(sketch, "E185", {"center": v(-21, 21) * mm, "radius": 1.65 * mm});
            skLineSegment(sketch, "E186", {"start": v(-23.83, 18.17) * mm, "end": v(-22.93, 17.27) * mm});
            skLineSegment(sketch, "E187", {"start": v(-21, 21) * mm, "end": v(0, 0) * mm, "construction": true});
            skLineSegment(sketch, "E188", {"start": v(-20, 10.2) * mm, "end": v(-20, 0) * mm});
            skPoint(sketch, "E189.visualSharp", {"position": v(-20, 14.34) * mm});
            skArc(sketch, "E189.filletArc", {"start": v(-20, 10.2) * mm, "mid": v(-20.76, 14.03) * mm, "end": v(-22.93, 17.27) * mm});
            skLineSegment(sketch, "E190", {"start": v(0, 0) * mm, "end": v(0, 0) * mm});
            skLineSegment(sketch, "E191.MirrorCS", {"start": v(20, 10.2) * mm, "end": v(20, 0) * mm});
            skPoint(sketch, "E192.MirrorP", {"position": v(20, 14.34) * mm});
            skLineSegment(sketch, "E193.MirrorCS", {"start": v(23.83, 18.17) * mm, "end": v(22.93, 17.27) * mm});
            skCircle(sketch, "E194.MirrorC", {"center": v(21, 21) * mm, "radius": 1.65 * mm});
            skLineSegment(sketch, "E195.MirrorCS", {"start": v(21, 21) * mm, "end": v(0, 0) * mm, "construction": true});
            skArc(sketch, "E196.MirrorCS", {"start": v(20, 10.2) * mm, "mid": v(20.76, 14.03) * mm, "end": v(22.93, 17.27) * mm});
            skLineSegment(sketch, "E197.MirrorCS", {"start": v(0, 36) * mm, "end": v(0, 0) * mm, "construction": true});
            skArc(sketch, "E198.MirrorCS", {"start": v(-20, -10.2) * mm, "mid": v(-20.76, -14.03) * mm, "end": v(-22.93, -17.27) * mm});
            skLineSegment(sketch, "E199.MirrorCS", {"start": v(-20, -10.2) * mm, "end": v(-20, 0) * mm});
            skLineSegment(sketch, "E200.MirrorCS", {"start": v(20, -10.2) * mm, "end": v(20, 0) * mm});
            skArc(sketch, "E201.MirrorCS", {"start": v(20, -10.2) * mm, "mid": v(20.76, -14.03) * mm, "end": v(22.93, -17.27) * mm});
            skLineSegment(sketch, "E202.MirrorCS", {"start": v(23.83, -18.17) * mm, "end": v(22.93, -17.27) * mm});
            skLineSegment(sketch, "E203.MirrorCS", {"start": v(-23.83, -18.17) * mm, "end": v(-22.93, -17.27) * mm});
            skArc(sketch, "E204.MirrorCS", {"start": v(23.83, -23.83) * mm, "mid": v(25, -21) * mm, "end": v(23.83, -18.17) * mm});
            skCircle(sketch, "E205.MirrorC", {"center": v(-21, -21) * mm, "radius": 1.65 * mm});
            skCircle(sketch, "E206.MirrorC", {"center": v(21, -21) * mm, "radius": 1.65 * mm});
            skLineSegment(sketch, "E207.bottom", {"start": v(-15.6, -23) * mm, "end": v(-14, -23) * mm});
            skLineSegment(sketch, "E207.top", {"start": v(-15.6, -28) * mm, "end": v(-14, -28) * mm});
            skLineSegment(sketch, "E207.left", {"start": v(-15.6, -23) * mm, "end": v(-15.6, -28) * mm});
            skLineSegment(sketch, "E207.right", {"start": v(-14, -23) * mm, "end": v(-14, -28) * mm});
            skLineSegment(sketch, "E208.MirrorCS", {"start": v(15.6, -28) * mm, "end": v(14, -28) * mm});
            skLineSegment(sketch, "E209.MirrorCS", {"start": v(14, -23) * mm, "end": v(14, -28) * mm});
            skLineSegment(sketch, "E210.MirrorCS", {"start": v(15.6, -23) * mm, "end": v(15.6, -28) * mm});
            skLineSegment(sketch, "E211.MirrorCS", {"start": v(15.6, -23) * mm, "end": v(14, -23) * mm});
            skLineSegment(sketch, "E212", {"start": v(0, 0) * mm, "end": v(-70.71, -70.71) * mm, "construction": true});
            skCircle(sketch, "E213", {"center": v(-70.71, -70.71) * mm, "radius": 64.25 * mm, "construction": true});
            skArc(sketch, "E214", {"start": v(-10.95, -42) * mm, "mid": v(-16.62, -32.37) * mm, "end": v(-23.83, -23.83) * mm});
            skArc(sketch, "E215", {"start": v(-23.83, -23.83) * mm, "mid": v(-25, -21) * mm, "end": v(-23.83, -18.17) * mm});
            skArc(sketch, "E216.MirrorCS", {"start": v(10.95, -42) * mm, "mid": v(16.62, -32.37) * mm, "end": v(23.83, -23.83) * mm});
            skLineSegment(sketch, "E217", {"start": v(-10.95, -42) * mm, "end": v(-8.74, -42) * mm});
            skLineSegment(sketch, "E218.trimOffspring", {"start": v(8.74, -42) * mm, "end": v(10.95, -42) * mm});
            skLineSegment(sketch, "E219", {"start": v(-3.75, 27.5) * mm, "end": v(-3.75, 25) * mm, "construction": true});
            skArc(sketch, "E220.0.startCap", {"start": v(-5, 27.5) * mm, "mid": v(-3.75, 28.75) * mm, "end": v(-2.5, 27.5) * mm});
            skArc(sketch, "E220.0.endCap", {"start": v(-2.5, 25) * mm, "mid": v(-3.75, 23.75) * mm, "end": v(-5, 25) * mm});
            skLineSegment(sketch, "E220.0.left", {"start": v(-2.5, 27.5) * mm, "end": v(-2.5, 25) * mm});
            skLineSegment(sketch, "E220.0.right", {"start": v(-5, 27.5) * mm, "end": v(-5, 25) * mm});
            skLineSegment(sketch, "E221.MirrorCS", {"start": v(5, 27.5) * mm, "end": v(5, 25) * mm});
            skArc(sketch, "E222.MirrorCS", {"start": v(5, 27.5) * mm, "mid": v(3.75, 28.75) * mm, "end": v(2.5, 27.5) * mm});
            skArc(sketch, "E223.MirrorCS", {"start": v(2.5, 25) * mm, "mid": v(3.75, 23.75) * mm, "end": v(5, 25) * mm});
            skLineSegment(sketch, "E224.MirrorCS", {"start": v(2.5, 27.5) * mm, "end": v(2.5, 25) * mm});
            skLineSegment(sketch, "E225.MirrorCS", {"start": v(3.75, 27.5) * mm, "end": v(3.75, 25) * mm, "construction": true});
            skLineSegment(sketch, "E226", {"start": v(-7.15, 38) * mm, "end": v(7.15, 38) * mm});
            skArc(sketch, "E227", {"start": v(-23.83, 18.17) * mm, "mid": v(-24.77, 22.33) * mm, "end": v(-21.42, 24.98) * mm});
            skArc(sketch, "E228", {"start": v(23.83, 18.17) * mm, "mid": v(24.77, 22.33) * mm, "end": v(21.42, 24.98) * mm});
            skArc(sketch, "E229", {"start": v(-21.42, 24.98) * mm, "mid": v(-13.38, 28.63) * mm, "end": v(-9.12, 36.36) * mm});
            skArc(sketch, "E230.MirrorCS", {"start": v(21.42, 24.98) * mm, "mid": v(13.38, 28.63) * mm, "end": v(9.12, 36.36) * mm});
            skArc(sketch, "E231", {"start": v(8.74, -42) * mm, "mid": v(0, -35.03) * mm, "end": v(-8.74, -42) * mm});
            skPoint(sketch, "E232.visualSharp", {"position": v(-8.91, 38) * mm});
            skArc(sketch, "E232.filletArc", {"start": v(-7.15, 38) * mm, "mid": v(-8.43, 37.54) * mm, "end": v(-9.12, 36.36) * mm});
            skPoint(sketch, "E233.visualSharp", {"position": v(8.91, 38) * mm});
            skArc(sketch, "E233.filletArc", {"start": v(9.12, 36.36) * mm, "mid": v(8.43, 37.54) * mm, "end": v(7.15, 38) * mm});
            skArc(sketch, "E234.0.1.0", {"start": v(2.5, 32) * mm, "mid": v(3.75, 30.75) * mm, "end": v(5, 32) * mm});
            skLineSegment(sketch, "E234.0.1.1", {"start": v(3.75, 34.5) * mm, "end": v(3.75, 32) * mm, "construction": true});
            skArc(sketch, "E234.0.1.2", {"start": v(5, 34.5) * mm, "mid": v(3.75, 35.75) * mm, "end": v(2.5, 34.5) * mm});
            skLineSegment(sketch, "E234.0.1.3", {"start": v(5, 34.5) * mm, "end": v(5, 32) * mm});
            skLineSegment(sketch, "E234.0.1.4", {"start": v(-2.5, 34.5) * mm, "end": v(-2.5, 32) * mm});
            skLineSegment(sketch, "E234.0.1.5", {"start": v(-3.75, 34.5) * mm, "end": v(-3.75, 32) * mm, "construction": true});
            skArc(sketch, "E234.0.1.6", {"start": v(-2.5, 32) * mm, "mid": v(-3.75, 30.75) * mm, "end": v(-5, 32) * mm});
            skLineSegment(sketch, "E234.0.1.7", {"start": v(2.5, 34.5) * mm, "end": v(2.5, 32) * mm});
            skLineSegment(sketch, "E234.0.1.8", {"start": v(-5, 34.5) * mm, "end": v(-5, 32) * mm});
            skArc(sketch, "E234.0.1.9", {"start": v(-5, 34.5) * mm, "mid": v(-3.75, 35.75) * mm, "end": v(-2.5, 34.5) * mm});
            skLineSegment(sketch, "E234.direction1", {"start": v(-5, 25) * mm, "end": v(20, 25) * mm, "construction": true});
            skLineSegment(sketch, "E234.direction2", {"start": v(-5, 25) * mm, "end": v(-5, 32) * mm, "construction": true});
            skSolve(sketch);
        }
        {
            var Q0;
            Q0=makeQuery(id+"F10.imprint","IMPRINT",FACE,{"disambiguationData":[TD([[makeQuery(id+"F10.imprint","IMPRINT",EDGE,{"derivedFrom":sQuery(id+"F10.wireOp",EDGE,"E185")}),-1.0]])]});
            extrude(context, id + "F11", {"entities" : qUnion([Q0]), "depth" : 1.5 * mm});
        }
        {
            var Q0;
            Q0=makeQuery(id+"F11.opExtrude","CAP_FACE",FACE,{"disambiguationData":[OSD([sQuery(id+"F10.wireOp",EDGE,"E185"),sQuery(id+"F10.wireOp",EDGE,"C1XNVG7k-0FuO-DmIR-nKNt-iijcf70ywYW7"),sQuery(id+"F10.wireOp",EDGE,"1JmxdRkD-XWPe-tDd6-sWuO-UiO5tpgJbU8n"),sQuery(id+"F10.wireOp",EDGE,"qC2pTZaY-QVpN-GFV0-oAhF-SKeQF19ME5D9"),sQuery(id+"F10.wireOp",EDGE,"E186"),sQuery(id+"F10.wireOp",EDGE,"E188"),sQuery(id+"F10.wireOp",EDGE,"E189.filletArc"),sQuery(id+"F10.wireOp",EDGE,"E191.MirrorCS"),sQuery(id+"F10.wireOp",EDGE,"7443f5ac-ebe8-482a-814f-4fc3a6a16acd2.MirrorCS"),sQuery(id+"F10.wireOp",EDGE,"E193.MirrorCS"),sQuery(id+"F10.wireOp",EDGE,"7443f5ac-ebe8-482a-814f-4fc3a6a16acd4.MirrorCS"),sQuery(id+"F10.wireOp",EDGE,"E194.MirrorC"),sQuery(id+"F10.wireOp",EDGE,"7443f5ac-ebe8-482a-814f-4fc3a6a16acd6.MirrorCS"),sQuery(id+"F10.wireOp",EDGE,"E196.MirrorCS"),sQuery(id+"F10.wireOp",EDGE,"E198.MirrorCS"),sQuery(id+"F10.wireOp",EDGE,"E199.MirrorCS"),sQuery(id+"F10.wireOp",EDGE,"E200.MirrorCS"),sQuery(id+"F10.wireOp",EDGE,"E201.MirrorCS"),sQuery(id+"F10.wireOp",EDGE,"E202.MirrorCS"),sQuery(id+"F10.wireOp",EDGE,"E203.MirrorCS"),sQuery(id+"F10.wireOp",EDGE,"920d5ffd-3ccc-4f48-bb8e-6c259681e9ea0.MirrorCS"),sQuery(id+"F10.wireOp",EDGE,"E204.MirrorCS"),sQuery(id+"F10.wireOp",EDGE,"6d739943-ed94-4d6a-83af-c7ee9b53e6000.MirrorCS"),sQuery(id+"F10.wireOp",EDGE,"92157b26-c4a0-4e89-9586-dcc7775d5ddd0.MirrorCS"),sQuery(id+"F10.wireOp",EDGE,"E205.MirrorC"),sQuery(id+"F10.wireOp",EDGE,"E206.MirrorC"),sQuery(id+"F10.wireOp",EDGE,"6LLzlCl9-pIkG-ylEb-rQc8-LpSHkL36GfJh"),sQuery(id+"F10.wireOp",EDGE,"BRovLQjg-58oc-8yov-hL1k-GmZUxygz8b3U"),sQuery(id+"F10.wireOp",EDGE,"45a8d127-23e0-4cab-910c-54c4c990bd860.MirrorCS"),sQuery(id+"F10.wireOp",EDGE,"s5xo5Asv-idW3-iZUK-O8kW-0OEmwKlhXYxH"),sQuery(id+"F10.wireOp",EDGE,"3ba12d3b-7b13-4584-9ad2-bd2aa17df9f10.MirrorCS"),sQuery(id+"F10.wireOp",EDGE,"E207.bottom"),sQuery(id+"F10.wireOp",EDGE,"E207.top"),sQuery(id+"F10.wireOp",EDGE,"E207.left"),sQuery(id+"F10.wireOp",EDGE,"E207.right"),sQuery(id+"F10.wireOp",EDGE,"E208.MirrorCS"),sQuery(id+"F10.wireOp",EDGE,"E209.MirrorCS"),sQuery(id+"F10.wireOp",EDGE,"E210.MirrorCS"),sQuery(id+"F10.wireOp",EDGE,"E211.MirrorCS")])],"isStart":false});
            var sketch = newSketch(context, id + "F12", { "sketchPlane" : qUnion([Q0])});
            skCircle(sketch, "E235", {"center": v(-14, -23.5) * mm, "radius": 0.5 * mm});
            skCircle(sketch, "E236", {"center": v(-15.6, -23.5) * mm, "radius": 0.5 * mm});
            skCircle(sketch, "E237", {"center": v(-15.6, -27.5) * mm, "radius": 0.5 * mm});
            skCircle(sketch, "E238", {"center": v(-14, -27.5) * mm, "radius": 0.5 * mm});
            skCircle(sketch, "E239.MirrorC", {"center": v(14, -27.5) * mm, "radius": 0.5 * mm});
            skCircle(sketch, "E240.MirrorC", {"center": v(15.6, -27.5) * mm, "radius": 0.5 * mm});
            skCircle(sketch, "E241.MirrorC", {"center": v(15.6, -23.5) * mm, "radius": 0.5 * mm});
            skCircle(sketch, "E242.MirrorC", {"center": v(14, -23.5) * mm, "radius": 0.5 * mm});
            skSolve(sketch);
        }
        {
            var Q0;
            Q0=qSketchRegion(id+"F12",true);
            extrude(context, id + "F13", {"entities" : qUnion([Q0]), "operationType" : NewBodyOperationType.REMOVE, "oppositeDirection" : true, "depth" : 25 * mm});
        }
        {
            var Q0;
            Q0=qCreatedBy(makeId("Top.planeOp"),FACE);
            var sketch = newSketch(context, id + "F14", { "sketchPlane" : qUnion([Q0])});
            skCircle(sketch, "E243", {"center": v(0, 0) * mm, "radius": 3.15 * mm});
            skCircle(sketch, "E244", {"center": v(0, 0) * mm, "radius": 1.25 * mm});
            skSolve(sketch);
        }
        {
            var Q0;
            Q0=makeQuery(id+"F14.imprint","IMPRINT",FACE,{"disambiguationData":[TD([[makeQuery(id+"F14.imprint","IMPRINT",EDGE,{"derivedFrom":sQuery(id+"F14.wireOp",EDGE,"E243")}),1.0]])]});
            extrude(context, id + "F15", {"entities" : qUnion([Q0]), "depth" : 30 * mm});
        }
        {
            var Q0;
            Q0=qCreatedBy(makeId("Top.planeOp"),FACE);
            var sketch = newSketch(context, id + "F16", { "sketchPlane" : qUnion([Q0])});
            skCircle(sketch, "E245", {"center": v(0, 0) * mm, "radius": 2.23 * mm});
            skCircle(sketch, "E246", {"center": v(0, 0) * mm, "radius": 1.25 * mm});
            skSolve(sketch);
        }
        {
            var Q0;
            Q0=makeQuery(id+"F16.imprint","IMPRINT",FACE,{"disambiguationData":[TD([[makeQuery(id+"F16.imprint","IMPRINT",EDGE,{"derivedFrom":sQuery(id+"F16.wireOp",EDGE,"E245")}),1.0]])]});
            extrude(context, id + "F17", {"entities" : qUnion([Q0]), "depth" : 1.5 * mm});
        }
        {
            var Q0;
            Q0=makeQuery(id+"F17.opExtrude","CAP_FACE",FACE,{"disambiguationData":[OSD([sQuery(id+"F16.wireOp",EDGE,"E245"),sQuery(id+"F16.wireOp",EDGE,"E246")])],"isStart":false});
            var sketch = newSketch(context, id + "F18", { "sketchPlane" : qUnion([Q0])});
            skCircle(sketch, "E247", {"center": v(0, 0) * mm, "radius": 2.75 * mm});
            skCircle(sketch, "E248", {"center": v(0, 0) * mm, "radius": 1.25 * mm});
            skSolve(sketch);
        }
        {
            var Q0;
            Q0=qSketchRegion(id+"F18",true);
            extrude(context, id + "F19", {"entities" : qUnion([Q0]), "operationType" : NewBodyOperationType.ADD, "depth" : 1.5 * mm});
        }
        {
            var Q0;
            Q0=makeQuery(id+"F3.opExtrude","SWEPT_EDGE",EDGE,{"disambiguationData":[OSD([sQuery(id+"F2.wireOp",EDGE,"E106"),sQuery(id+"F2.wireOp",EDGE,"E107")])]});
            var Q1;
            Q1=makeQuery(id+"F3.opExtrude","SWEPT_EDGE",EDGE,{"disambiguationData":[OSD([sQuery(id+"F2.wireOp",EDGE,"E108.MirrorCS"),sQuery(id+"F2.wireOp",EDGE,"E109.MirrorCS")])]});
            fillet(context, id + "F20", {"entities" : qUnion([Q0, Q1]), "radius" : 2 * mm, "tangentPropagation" : true, "allowEdgeOverflow" : false});
        }
        {
            var Q0;
            Q0=qCreatedBy(makeId("Right.planeOp"),FACE);
            var sketch = newSketch(context, id + "F21", { "sketchPlane" : qUnion([Q0])});
            skLineSegment(sketch, "E249.top", {"start": v(-30.4, -1.5) * mm, "end": v(-25.5, -1.5) * mm});
            skLineSegment(sketch, "E249.left", {"start": v(-30.4, 0) * mm, "end": v(-30.4, -1.5) * mm});
            skLineSegment(sketch, "E249.right", {"start": v(-25.5, 0) * mm, "end": v(-25.5, -1.5) * mm});
            skLineSegment(sketch, "E250.bottom", {"start": v(-27.9, 37) * mm, "end": v(-23, 37) * mm});
            skLineSegment(sketch, "E250.top", {"start": v(-27.9, 35.5) * mm, "end": v(-23, 35.5) * mm, "construction": true});
            skLineSegment(sketch, "E250.left", {"start": v(-27.9, 37) * mm, "end": v(-27.9, 35.5) * mm});
            skLineSegment(sketch, "E250.right", {"start": v(-23, 37) * mm, "end": v(-23, 35.5) * mm});
            skLineSegment(sketch, "E251", {"start": v(-23, 35.5) * mm, "end": v(-19, 35.5) * mm});
            skLineSegment(sketch, "E252", {"start": v(-27.9, 35.5) * mm, "end": v(-30.9, 35.5) * mm});
            skLineSegment(sketch, "E253", {"start": v(-25.5, 0) * mm, "end": v(-25.5, 5.5) * mm});
            skLineSegment(sketch, "E254", {"start": v(-25.5, 5.5) * mm, "end": v(-19, 5.5) * mm});
            skPoint(sketch, "E255.visualSharp", {"position": v(-25.5, 5.5) * mm});
            skLineSegment(sketch, "E256", {"start": v(-30.4, 0) * mm, "end": v(-35.4, 0) * mm});
            skLineSegment(sketch, "E257", {"start": v(-19, 35.5) * mm, "end": v(-19, 5.5) * mm});
            skArc(sketch, "E258", {"start": v(-30.9, 35.5) * mm, "mid": v(-35.86, 18.1) * mm, "end": v(-35.4, 0) * mm});
            skCircle(sketch, "E259", {"center": v(-33.5, 10.8) * mm, "radius": 1.55 * mm});
            skLineSegment(sketch, "E260", {"start": v(-41.53, 0.15) * mm, "end": v(-21.61, 16.86) * mm, "construction": true});
            skLineSegment(sketch, "E261", {"start": v(-33.5, 10.8) * mm, "end": v(-31.57, 8.5) * mm, "construction": true});
            skCircle(sketch, "E262", {"center": v(-31.6, 12) * mm, "radius": 1.55 * mm});
            skLineSegment(sketch, "E263", {"start": v(-31.6, 12) * mm, "end": v(-29.3, 10.07) * mm, "construction": true});
            skLineSegment(sketch, "E264", {"start": v(-37.66, 0.11) * mm, "end": v(-20.95, 20.03) * mm, "construction": true});
            skCircle(sketch, "E265", {"center": v(-29.6, 13.4) * mm, "radius": 1.55 * mm});
            skLineSegment(sketch, "E266", {"start": v(-33.5, 0.64) * mm, "end": v(-20.5, 23.16) * mm, "construction": true});
            skLineSegment(sketch, "E267", {"start": v(-29.6, 13.4) * mm, "end": v(-27, 11.9) * mm, "construction": true});
            skCircle(sketch, "E268", {"center": v(-27.9, 14.8) * mm, "radius": 1.55 * mm});
            skLineSegment(sketch, "E269", {"start": v(-27.9, 14.8) * mm, "end": v(-25.08, 13.77) * mm, "construction": true});
            skLineSegment(sketch, "E270", {"start": v(-29.53, 1.56) * mm, "end": v(-20.63, 25.99) * mm, "construction": true});
            skSolve(sketch);
        }
        {
            var Q0;
            Q0=makeQuery(id+"F21.imprint","IMPRINT",FACE,{"disambiguationData":[TD([[makeQuery(id+"F21.imprint","IMPRINT",EDGE,{"derivedFrom":sQuery(id+"F21.wireOp",EDGE,"E249.top")}),1.0]])]});
            extrude(context, id + "F22", {"entities" : qUnion([Q0]), "depth" : 1.5 * mm});
        }
        {
            var Q0;
            Q0=makeQuery(id+"F22.opExtrude","CAP_FACE",FACE,{"disambiguationData":[OSD([sQuery(id+"F21.wireOp",EDGE,"E249.top"),sQuery(id+"F21.wireOp",EDGE,"E249.left"),sQuery(id+"F21.wireOp",EDGE,"E249.right"),sQuery(id+"F21.wireOp",EDGE,"E250.bottom"),sQuery(id+"F21.wireOp",EDGE,"E250.left"),sQuery(id+"F21.wireOp",EDGE,"E250.right"),sQuery(id+"F21.wireOp",EDGE,"E251"),sQuery(id+"F21.wireOp",EDGE,"E252"),sQuery(id+"F21.wireOp",EDGE,"E253"),sQuery(id+"F21.wireOp",EDGE,"E254"),sQuery(id+"F21.wireOp",EDGE,"E256"),sQuery(id+"F21.wireOp",EDGE,"E257"),sQuery(id+"F21.wireOp",EDGE,"E258"),sQuery(id+"F21.wireOp",EDGE,"IlX3JSMu-NUec-YmUJ-kGKA-v2RqxQZpXFZG"),sQuery(id+"F21.wireOp",EDGE,"QqSHGALd-vgMH-CsCO-2UtY-GNjF0gbNKMfq"),sQuery(id+"F21.wireOp",EDGE,"c9571d5d-53fe-49e0-8d75-11ff31d18f6d.1.0.0"),sQuery(id+"F21.wireOp",EDGE,"c9571d5d-53fe-49e0-8d75-11ff31d18f6d.2.0.0"),sQuery(id+"F21.wireOp",EDGE,"125c3161-0d2e-4c84-b0d3-5869db5af3f9.trimOffspring"),sQuery(id+"F21.wireOp",EDGE,"ea2af63f-a69e-4b98-8f0a-1ea5ec80e0f0.1.0.0"),sQuery(id+"F21.wireOp",EDGE,"8b0a454f-8ec5-4ccb-b880-c8bcff42a064.trimOffspring"),sQuery(id+"F21.wireOp",EDGE,"b1a4fc6e-4469-44ba-9b3a-8baa4c264c5c.trimOffspring"),sQuery(id+"F21.wireOp",EDGE,"E259"),sQuery(id+"F21.wireOp",EDGE,"baf5fba7-d95c-4aec-8581-47ca1ced992e.0.3.0"),sQuery(id+"F21.wireOp",EDGE,"baf5fba7-d95c-4aec-8581-47ca1ced992e.0.4.0"),sQuery(id+"F21.wireOp",EDGE,"f055a136-d7f1-46da-b909-f311c71264d7.trimOffspring"),sQuery(id+"F21.wireOp",EDGE,"9be788b4-47e9-4e63-ba09-159407b564ad.trimOffspring"),sQuery(id+"F21.wireOp",EDGE,"186d221a-cc9f-4302-9d80-a85e1b2c8977.trimOffspring"),sQuery(id+"F21.wireOp",EDGE,"oNhZRw74-Onx2-UYVr-j9Fp-hqOf6hEBPdf1")])],"isStart":false});
            var sketch = newSketch(context, id + "F23", { "sketchPlane" : qUnion([Q0])});
            skLineSegment(sketch, "E271.bottom", {"start": v(-19, 5.5) * mm, "end": v(-22.5, 5.5) * mm});
            skLineSegment(sketch, "E271.top", {"start": v(-19, 13.5) * mm, "end": v(-20.5, 13.5) * mm});
            skLineSegment(sketch, "E271.left", {"start": v(-19, 5.5) * mm, "end": v(-19, 13.5) * mm});
            skLineSegment(sketch, "E271.right", {"start": v(-22.5, 5.5) * mm, "end": v(-22.5, 11.5) * mm});
            skPoint(sketch, "E272.visualSharp", {"position": v(-22.5, 13.5) * mm});
            skArc(sketch, "E272.filletArc", {"start": v(-20.5, 13.5) * mm, "mid": v(-21.91, 12.91) * mm, "end": v(-22.5, 11.5) * mm});
            skArc(sketch, "E273", {"start": v(-26.57, 27.48) * mm, "mid": v(-29.06, 26.8) * mm, "end": v(-28.14, 24.37) * mm});
            skArc(sketch, "E274", {"start": v(-22.86, 24.37) * mm, "mid": v(-21.94, 26.8) * mm, "end": v(-24.43, 27.48) * mm});
            skArc(sketch, "E275", {"start": v(-26.95, 23.04) * mm, "mid": v(-25.5, 21.94) * mm, "end": v(-24.05, 23.04) * mm});
            skArc(sketch, "E276", {"start": v(-26.57, 27.48) * mm, "mid": v(-25.5, 27.17) * mm, "end": v(-24.43, 27.48) * mm});
            skArc(sketch, "E277", {"start": v(-26.95, 23.04) * mm, "mid": v(-27.39, 23.85) * mm, "end": v(-28.14, 24.37) * mm});
            skArc(sketch, "E278", {"start": v(-22.86, 24.37) * mm, "mid": v(-23.61, 23.85) * mm, "end": v(-24.05, 23.04) * mm});
            skLineSegment(sketch, "E279", {"start": v(-27.5, 26) * mm, "end": v(-23.5, 26) * mm, "construction": true});
            skLineSegment(sketch, "E280", {"start": v(-25.5, 23.44) * mm, "end": v(-25.5, 26) * mm, "construction": true});
            skSolve(sketch);
        }
        {
            var Q0;
            Q0=qSketchRegion(id+"F23",true);
            extrude(context, id + "F24", {"entities" : qUnion([Q0]), "operationType" : NewBodyOperationType.REMOVE, "oppositeDirection" : true, "depth" : 25 * mm});
        }
        {
            var Q0;
            Q0=makeQuery(id+"F22.opExtrude","CAP_FACE",FACE,{"disambiguationData":[OSD([sQuery(id+"F21.wireOp",EDGE,"E249.top"),sQuery(id+"F21.wireOp",EDGE,"E249.left"),sQuery(id+"F21.wireOp",EDGE,"E249.right"),sQuery(id+"F21.wireOp",EDGE,"E250.bottom"),sQuery(id+"F21.wireOp",EDGE,"E250.left"),sQuery(id+"F21.wireOp",EDGE,"E250.right"),sQuery(id+"F21.wireOp",EDGE,"E251"),sQuery(id+"F21.wireOp",EDGE,"E252"),sQuery(id+"F21.wireOp",EDGE,"E253"),sQuery(id+"F21.wireOp",EDGE,"E254"),sQuery(id+"F21.wireOp",EDGE,"E256"),sQuery(id+"F21.wireOp",EDGE,"E257"),sQuery(id+"F21.wireOp",EDGE,"E258"),sQuery(id+"F21.wireOp",EDGE,"IlX3JSMu-NUec-YmUJ-kGKA-v2RqxQZpXFZG"),sQuery(id+"F21.wireOp",EDGE,"QqSHGALd-vgMH-CsCO-2UtY-GNjF0gbNKMfq"),sQuery(id+"F21.wireOp",EDGE,"c9571d5d-53fe-49e0-8d75-11ff31d18f6d.1.0.0"),sQuery(id+"F21.wireOp",EDGE,"c9571d5d-53fe-49e0-8d75-11ff31d18f6d.2.0.0"),sQuery(id+"F21.wireOp",EDGE,"125c3161-0d2e-4c84-b0d3-5869db5af3f9.trimOffspring"),sQuery(id+"F21.wireOp",EDGE,"ea2af63f-a69e-4b98-8f0a-1ea5ec80e0f0.1.0.0"),sQuery(id+"F21.wireOp",EDGE,"8b0a454f-8ec5-4ccb-b880-c8bcff42a064.trimOffspring"),sQuery(id+"F21.wireOp",EDGE,"b1a4fc6e-4469-44ba-9b3a-8baa4c264c5c.trimOffspring"),sQuery(id+"F21.wireOp",EDGE,"E259"),sQuery(id+"F21.wireOp",EDGE,"baf5fba7-d95c-4aec-8581-47ca1ced992e.0.3.0"),sQuery(id+"F21.wireOp",EDGE,"baf5fba7-d95c-4aec-8581-47ca1ced992e.0.4.0"),sQuery(id+"F21.wireOp",EDGE,"f055a136-d7f1-46da-b909-f311c71264d7.trimOffspring"),sQuery(id+"F21.wireOp",EDGE,"9be788b4-47e9-4e63-ba09-159407b564ad.trimOffspring"),sQuery(id+"F21.wireOp",EDGE,"186d221a-cc9f-4302-9d80-a85e1b2c8977.trimOffspring"),sQuery(id+"F21.wireOp",EDGE,"oNhZRw74-Onx2-UYVr-j9Fp-hqOf6hEBPdf1")])],"isStart":false});
            var sketch = newSketch(context, id + "F25", { "sketchPlane" : qUnion([Q0])});
            skCircle(sketch, "E281", {"center": v(-28.4, 35.5) * mm, "radius": 0.5 * mm});
            skCircle(sketch, "E282", {"center": v(-22.5, 35.5) * mm, "radius": 0.5 * mm});
            skCircle(sketch, "E283", {"center": v(-30.9, 0) * mm, "radius": 0.5 * mm});
            skCircle(sketch, "E284", {"center": v(-25, 5.5) * mm, "radius": 0.5 * mm});
            skSolve(sketch);
        }
        {
            var Q0;
            Q0=qSketchRegion(id+"F25",true);
            extrude(context, id + "F26", {"entities" : qUnion([Q0]), "operationType" : NewBodyOperationType.REMOVE, "oppositeDirection" : true, "depth" : 25 * mm});
        }
        {
            var Q0;
            Q0=makeQuery(id+"F1.opExtrude","SWEPT_EDGE",EDGE,{"disambiguationData":[OSD([sQuery(id+"F0.wireOp",EDGE,"E11"),sQuery(id+"F0.wireOp",EDGE,"E26")])]});
            var Q1;
            Q1=makeQuery(id+"F1.opExtrude","SWEPT_EDGE",EDGE,{"disambiguationData":[OSD([sQuery(id+"F0.wireOp",EDGE,"E12.MirrorCS"),sQuery(id+"F0.wireOp",EDGE,"E26")])]});
            var Q2;
            Q2=makeQuery(id+"F1.opExtrude","SWEPT_EDGE",EDGE,{"disambiguationData":[OSD([sQuery(id+"F0.wireOp",EDGE,"E18.MirrorCS"),sQuery(id+"F0.wireOp",EDGE,"E40.MirrorCS")])]});
            var Q3;
            Q3=makeQuery(id+"F1.opExtrude","SWEPT_EDGE",EDGE,{"disambiguationData":[OSD([sQuery(id+"F0.wireOp",EDGE,"E17.MirrorCS"),sQuery(id+"F0.wireOp",EDGE,"E40.MirrorCS")])]});
            fillet(context, id + "F27", {"entities" : qUnion([Q0, Q1, Q2, Q3]), "radius" : 6.66 * mm, "tangentPropagation" : true, "allowEdgeOverflow" : false});
        }
        {
            var Q0;
            Q0=qCreatedBy(makeId("Top.planeOp"),FACE);
            var sketch = newSketch(context, id + "F28", { "sketchPlane" : qUnion([Q0])});
            skCircle(sketch, "E285", {"center": v(28, -8.5) * mm, "radius": 6.25 * mm});
            skCircle(sketch, "E286", {"center": v(28, -8.5) * mm, "radius": 3.25 * mm});
            skSolve(sketch);
        }
        {
            var Q0;
            Q0=makeQuery(id+"F28.imprint","IMPRINT",FACE,{"disambiguationData":[TD([[makeQuery(id+"F28.imprint","IMPRINT",EDGE,{"derivedFrom":sQuery(id+"F28.wireOp",EDGE,"E285")}),1.0]])]});
            extrude(context, id + "F29", {"entities" : qUnion([Q0]), "operationType" : NewBodyOperationType.ADD, "depth" : 1.5 * mm});
        }
        {
            var Q0;
            Q0=makeQuery(id+"F22.opExtrude","CAP_FACE",FACE,{"disambiguationData":[OSD([sQuery(id+"F21.wireOp",EDGE,"E249.top"),sQuery(id+"F21.wireOp",EDGE,"E249.left"),sQuery(id+"F21.wireOp",EDGE,"E249.right"),sQuery(id+"F21.wireOp",EDGE,"E250.bottom"),sQuery(id+"F21.wireOp",EDGE,"E250.left"),sQuery(id+"F21.wireOp",EDGE,"E250.right"),sQuery(id+"F21.wireOp",EDGE,"E251"),sQuery(id+"F21.wireOp",EDGE,"E252"),sQuery(id+"F21.wireOp",EDGE,"E253"),sQuery(id+"F21.wireOp",EDGE,"E254"),sQuery(id+"F21.wireOp",EDGE,"E256"),sQuery(id+"F21.wireOp",EDGE,"E257"),sQuery(id+"F21.wireOp",EDGE,"E258"),sQuery(id+"F21.wireOp",EDGE,"E259"),sQuery(id+"F21.wireOp",EDGE,"E262"),sQuery(id+"F21.wireOp",EDGE,"E265"),sQuery(id+"F21.wireOp",EDGE,"E268")])],"isStart":false});
            var sketch = newSketch(context, id + "F30", { "sketchPlane" : qUnion([Q0])});
            skCircle(sketch, "E287", {"center": v(-24, 16) * mm, "radius": 1.55 * mm});
            skSolve(sketch);
        }
        {
            var Q0;
            Q0=qSketchRegion(id+"F30",true);
            extrude(context, id + "F31", {"entities" : qUnion([Q0]), "operationType" : NewBodyOperationType.REMOVE, "oppositeDirection" : true, "depth" : 25 * mm});
        }
        {
            var Q0;
            Q0=makeQuery(id+"F29.boolean.opBoolean","INTERSECT",EDGE,{"derivedFrom":[makeQuery(id+"F1.opExtrude","SWEPT_FACE",FACE,{"disambiguationData":[OSD([sQuery(id+"F0.wireOp",EDGE,"E40.MirrorCS")])]}),makeQuery(id+"F29.opExtrude","SWEPT_FACE",FACE,{"disambiguationData":[OSD([sQuery(id+"F28.wireOp",EDGE,"E285")])]})]});
            fillet(context, id + "F32", {"entities" : qUnion([Q0]), "radius" : 5 * mm, "tangentPropagation" : true, "allowEdgeOverflow" : false});
        }
        {
            var Q0;
            Q0=qCreatedBy(makeId("Top.planeOp"),FACE);
            var sketch = newSketch(context, id + "F33", { "sketchPlane" : qUnion([Q0])});
            skArc(sketch, "E288", {"start": v(28.69, -14.71) * mm, "mid": v(27.13, -15.77) * mm, "end": v(27.15, -17.66) * mm});
            skLineSegment(sketch, "E289", {"start": v(27.15, -17.66) * mm, "end": v(21.49, -12.71) * mm});
            skLineSegment(sketch, "E290", {"start": v(21.49, -12.71) * mm, "end": v(28.69, -12.71) * mm});
            skLineSegment(sketch, "E291", {"start": v(28.69, -12.71) * mm, "end": v(28.69, -14.71) * mm});
            skSolve(sketch);
        }
        {
            var Q0;
            Q0=qSketchRegion(id+"F33",true);
            extrude(context, id + "F34", {"entities" : qUnion([Q0]), "operationType" : NewBodyOperationType.ADD, "depth" : 1.5 * mm});
        }
        {
            var Q0;
            Q0=qCreatedBy(makeId("Right.planeOp"),FACE);
            var sketch = newSketch(context, id + "F35", { "sketchPlane" : qUnion([Q0])});
            skLineSegment(sketch, "E292.bottom", {"start": v(-4.25, 24) * mm, "end": v(-4.25, 24) * mm});
            skLineSegment(sketch, "E292.top", {"start": v(-4.25, 6) * mm, "end": v(-4.25, 6) * mm});
            skLineSegment(sketch, "E292.left", {"start": v(-4.25, 24) * mm, "end": v(-4.25, 6) * mm});
            skLineSegment(sketch, "E292.right", {"start": v(-2.25, 22) * mm, "end": v(-2.25, 8) * mm});
            skPoint(sketch, "E293.visualSharp", {"position": v(-2.25, 24) * mm});
            skArc(sketch, "E293.filletArc", {"start": v(-2.25, 22) * mm, "mid": v(-2.84, 23.41) * mm, "end": v(-4.25, 24) * mm});
            skPoint(sketch, "E294.visualSharp", {"position": v(-2.25, 6) * mm});
            skArc(sketch, "E294.filletArc", {"start": v(-4.25, 6) * mm, "mid": v(-2.84, 6.59) * mm, "end": v(-2.25, 8) * mm});
            skLineSegment(sketch, "E295", {"start": v(0, 0) * mm, "end": v(0, 39.06) * mm, "construction": true});
            skSolve(sketch);
        }
        {
            var Q0;
            Q0=qSketchRegion(id+"F35",true);
            var Q1;
            Q1=sQuery(id+"F35.wireOp",EDGE,"E295");
            revolve(context, id + "F36", {"operationType" : NewBodyOperationType.REMOVE, "entities" : qUnion([Q0]), "axis" : qUnion([Q1]), "revolveType" : RevolveType.FULL, "oppositeDirection" : true});
        }
        {
            var Q0;
            Q0=makeQuery(id+"F36.boolean.opBoolean","INTERSECT",EDGE,{"derivedFrom":[makeQuery(id+"F15.opExtrude","SWEPT_FACE",FACE,{"disambiguationData":[OSD([sQuery(id+"F14.wireOp",EDGE,"E243")])]}),makeQuery(id+"F36.opRevolve","SWEPT_FACE",FACE,{"disambiguationData":[OSD([sQuery(id+"F35.wireOp",EDGE,"E293.filletArc")])]})]});
            var Q1;
            Q1=makeQuery(id+"F36.boolean.opBoolean","INTERSECT",EDGE,{"derivedFrom":[makeQuery(id+"F15.opExtrude","SWEPT_FACE",FACE,{"disambiguationData":[OSD([sQuery(id+"F14.wireOp",EDGE,"E243")])]}),makeQuery(id+"F36.opRevolve","SWEPT_FACE",FACE,{"disambiguationData":[OSD([sQuery(id+"F35.wireOp",EDGE,"E294.filletArc")])]})]});
            fillet(context, id + "F37", {"entities" : qUnion([Q0, Q1]), "radius" : 2 * mm, "tangentPropagation" : true, "allowEdgeOverflow" : false});
        }
        {
            var Q0;
            Q0=makeQuery(id+"F3.opExtrude","SWEPT_EDGE",EDGE,{"disambiguationData":[OSD([sQuery(id+"F2.wireOp",EDGE,"E119"),sQuery(id+"F2.wireOp",EDGE,"E120")])]});
            var Q1;
            Q1=makeQuery(id+"F3.opExtrude","SWEPT_EDGE",EDGE,{"disambiguationData":[OSD([sQuery(id+"F2.wireOp",EDGE,"E121.MirrorCS"),sQuery(id+"F2.wireOp",EDGE,"E122.MirrorCS")])]});
            fillet(context, id + "F38", {"entities" : qUnion([Q0, Q1]), "radius" : 2 * mm, "tangentPropagation" : true, "allowEdgeOverflow" : false});
        }
        {
            var Q0;
            Q0=makeQuery(id+"F3.opExtrude","CAP_FACE",FACE,{"disambiguationData":[OSD([sQuery(id+"F2.wireOp",EDGE,"E73"),sQuery(id+"F2.wireOp",EDGE,"E74"),sQuery(id+"F2.wireOp",EDGE,"E75"),sQuery(id+"F2.wireOp",EDGE,"E76"),sQuery(id+"F2.wireOp",EDGE,"E77.filletArc"),sQuery(id+"F2.wireOp",EDGE,"E79.MirrorCS"),sQuery(id+"F2.wireOp",EDGE,"E80.MirrorCS"),sQuery(id+"F2.wireOp",EDGE,"E81.MirrorCS"),sQuery(id+"F2.wireOp",EDGE,"E82.MirrorC"),sQuery(id+"F2.wireOp",EDGE,"E83.MirrorC"),sQuery(id+"F2.wireOp",EDGE,"E86.MirrorCS"),sQuery(id+"F2.wireOp",EDGE,"E87.MirrorCS"),sQuery(id+"F2.wireOp",EDGE,"E88.MirrorCS"),sQuery(id+"F2.wireOp",EDGE,"E89.MirrorCS"),sQuery(id+"F2.wireOp",EDGE,"E91.MirrorC"),sQuery(id+"F2.wireOp",EDGE,"E92.MirrorC"),sQuery(id+"F2.wireOp",EDGE,"E93.MirrorCS"),sQuery(id+"F2.wireOp",EDGE,"E94.MirrorC"),sQuery(id+"F2.wireOp",EDGE,"E95.MirrorC"),sQuery(id+"F2.wireOp",EDGE,"E96.MirrorCS"),sQuery(id+"F2.wireOp",EDGE,"E97.MirrorCS"),sQuery(id+"F2.wireOp",EDGE,"E98.MirrorCS"),sQuery(id+"F2.wireOp",EDGE,"E99.bottom"),sQuery(id+"F2.wireOp",EDGE,"E99.top"),sQuery(id+"F2.wireOp",EDGE,"E99.left"),sQuery(id+"F2.wireOp",EDGE,"E99.right"),sQuery(id+"F2.wireOp",EDGE,"E100.MirrorCS"),sQuery(id+"F2.wireOp",EDGE,"E101.MirrorCS"),sQuery(id+"F2.wireOp",EDGE,"E102.MirrorCS"),sQuery(id+"F2.wireOp",EDGE,"E103.MirrorCS"),sQuery(id+"F2.wireOp",EDGE,"E106"),sQuery(id+"F2.wireOp",EDGE,"E107"),sQuery(id+"F2.wireOp",EDGE,"E108.MirrorCS"),sQuery(id+"F2.wireOp",EDGE,"E109.MirrorCS"),sQuery(id+"F2.wireOp",EDGE,"E110.filletArc"),sQuery(id+"F2.wireOp",EDGE,"E111.filletArc"),sQuery(id+"F2.wireOp",EDGE,"E112"),sQuery(id+"F2.wireOp",EDGE,"E114.MirrorCS"),sQuery(id+"F2.wireOp",EDGE,"E115.MirrorCS"),sQuery(id+"F2.wireOp",EDGE,"E116.MirrorCS"),sQuery(id+"F2.wireOp",EDGE,"E119"),sQuery(id+"F2.wireOp",EDGE,"E120"),sQuery(id+"F2.wireOp",EDGE,"E121.MirrorCS"),sQuery(id+"F2.wireOp",EDGE,"E122.MirrorCS"),sQuery(id+"F2.wireOp",EDGE,"bcf1264d-b733-40b0-8774-b1950e08d1530.MirrorCS"),sQuery(id+"F2.wireOp",EDGE,"9af283ad-2154-46af-ae04-832c548851d70.MirrorCS"),sQuery(id+"F2.wireOp",EDGE,"E123"),sQuery(id+"F2.wireOp",EDGE,"E124.MirrorCS"),sQuery(id+"F2.wireOp",EDGE,"E125.filletArc"),sQuery(id+"F2.wireOp",EDGE,"E126.filletArc"),sQuery(id+"F2.wireOp",EDGE,"vuY6w2it-mn66-yzEo-Y1Tz-2XmqXBiDKGcJ")])],"isStart":false});
            var sketch = newSketch(context, id + "F39", { "sketchPlane" : qUnion([Q0])});
            skLineSegment(sketch, "E296", {"start": v(-4.5, 34) * mm, "end": v(-4.5, 31) * mm, "construction": true});
            skArc(sketch, "E297.0.startCap", {"start": v(-6, 34) * mm, "mid": v(-4.5, 35.5) * mm, "end": v(-3, 34) * mm});
            skArc(sketch, "E297.0.endCap", {"start": v(-3, 31) * mm, "mid": v(-4.5, 29.5) * mm, "end": v(-6, 31) * mm});
            skLineSegment(sketch, "E297.0.left", {"start": v(-3, 34) * mm, "end": v(-3, 31) * mm});
            skLineSegment(sketch, "E297.0.right", {"start": v(-6, 34) * mm, "end": v(-6, 31) * mm});
            skArc(sketch, "E298.MirrorCS", {"start": v(3, 31) * mm, "mid": v(4.5, 29.5) * mm, "end": v(6, 31) * mm});
            skLineSegment(sketch, "E299.MirrorCS", {"start": v(4.5, 34) * mm, "end": v(4.5, 31) * mm, "construction": true});
            skLineSegment(sketch, "E300.MirrorCS", {"start": v(3, 34) * mm, "end": v(3, 31) * mm});
            skArc(sketch, "E301.MirrorCS", {"start": v(6, 34) * mm, "mid": v(4.5, 35.5) * mm, "end": v(3, 34) * mm});
            skLineSegment(sketch, "E302.MirrorCS", {"start": v(6, 34) * mm, "end": v(6, 31) * mm});
            skSolve(sketch);
        }
        {
            var Q0;
            Q0=qSketchRegion(id+"F39",true);
            extrude(context, id + "F40", {"entities" : qUnion([Q0]), "operationType" : NewBodyOperationType.REMOVE, "oppositeDirection" : true, "depth" : 25 * mm});
        }
        {
            var Q0;
            Q0=makeQuery(id+"F22.opExtrude","SWEPT_EDGE",EDGE,{"disambiguationData":[OSD([sQuery(id+"F21.wireOp",EDGE,"E256"),sQuery(id+"F21.wireOp",EDGE,"E258")])]});
            chamfer(context, id + "F41", {"entities" : qUnion([Q0]), "width" : 2 * mm, "tangentPropagation" : true});
        }
        {
            var Q0;
            Q0=qCreatedBy(makeId("Top.planeOp"),FACE);
            var sketch = newSketch(context, id + "F42", { "sketchPlane" : qUnion([Q0])});
            skCircle(sketch, "E303", {"center": v(-21, 21) * mm, "radius": 1.65 * mm});
            skLineSegment(sketch, "E304", {"start": v(-3.75, 27.5) * mm, "end": v(-3.75, 25) * mm, "construction": true});
            skArc(sketch, "E305.0.startCap", {"start": v(-5, 27.5) * mm, "mid": v(-3.75, 28.75) * mm, "end": v(-2.5, 27.5) * mm});
            skArc(sketch, "E305.0.endCap", {"start": v(-2.5, 25) * mm, "mid": v(-3.75, 23.75) * mm, "end": v(-5, 25) * mm});
            skLineSegment(sketch, "E305.0.left", {"start": v(-2.5, 27.5) * mm, "end": v(-2.5, 25) * mm});
            skLineSegment(sketch, "E305.0.right", {"start": v(-5, 27.5) * mm, "end": v(-5, 25) * mm});
            skArc(sketch, "E306", {"start": v(-21.98, 24.88) * mm, "mid": v(-24.97, 20.5) * mm, "end": v(-21, 17) * mm});
            skLineSegment(sketch, "E307", {"start": v(-12.5, 30) * mm, "end": v(12.5, 30) * mm, "construction": true});
            skArc(sketch, "E308", {"start": v(-21.98, 24.88) * mm, "mid": v(-16.92, 26.85) * mm, "end": v(-12.5, 30) * mm});
            skLineSegment(sketch, "E309", {"start": v(-21, 17) * mm, "end": v(0, 17) * mm});
            skArc(sketch, "E310.MirrorCS", {"start": v(21.98, 24.88) * mm, "mid": v(16.92, 26.85) * mm, "end": v(12.5, 30) * mm});
            skArc(sketch, "E311.MirrorCS", {"start": v(21.98, 24.88) * mm, "mid": v(24.97, 20.5) * mm, "end": v(21, 17) * mm});
            skLineSegment(sketch, "E312.MirrorCS", {"start": v(21, 17) * mm, "end": v(0, 17) * mm});
            skLineSegment(sketch, "E313.MirrorCS", {"start": v(3.75, 27.5) * mm, "end": v(3.75, 25) * mm, "construction": true});
            skArc(sketch, "E314.MirrorCS", {"start": v(5, 27.5) * mm, "mid": v(3.75, 28.75) * mm, "end": v(2.5, 27.5) * mm});
            skLineSegment(sketch, "E315.MirrorCS", {"start": v(5, 27.5) * mm, "end": v(5, 25) * mm});
            skLineSegment(sketch, "E316.MirrorCS", {"start": v(2.5, 27.5) * mm, "end": v(2.5, 25) * mm});
            skArc(sketch, "E317.MirrorCS", {"start": v(2.5, 25) * mm, "mid": v(3.75, 23.75) * mm, "end": v(5, 25) * mm});
            skLineSegment(sketch, "E318", {"start": v(-3.75, 32.5) * mm, "end": v(-3.75, 35) * mm, "construction": true});
            skArc(sketch, "E319.0.startCap", {"start": v(-2.5, 32.5) * mm, "mid": v(-3.75, 31.25) * mm, "end": v(-5, 32.5) * mm});
            skArc(sketch, "E319.0.endCap", {"start": v(-5, 35) * mm, "mid": v(-3.75, 36.25) * mm, "end": v(-2.5, 35) * mm});
            skLineSegment(sketch, "E319.0.left", {"start": v(-5, 32.5) * mm, "end": v(-5, 35) * mm});
            skLineSegment(sketch, "E319.0.right", {"start": v(-2.5, 32.5) * mm, "end": v(-2.5, 35) * mm});
            skLineSegment(sketch, "E320.MirrorCS", {"start": v(2.5, 32.5) * mm, "end": v(2.5, 35) * mm});
            skLineSegment(sketch, "E321.MirrorCS", {"start": v(3.75, 32.5) * mm, "end": v(3.75, 35) * mm, "construction": true});
            skArc(sketch, "E322.MirrorCS", {"start": v(2.5, 32.5) * mm, "mid": v(3.75, 31.25) * mm, "end": v(5, 32.5) * mm});
            skLineSegment(sketch, "E323.MirrorCS", {"start": v(5, 32.5) * mm, "end": v(5, 35) * mm});
            skArc(sketch, "E324.MirrorCS", {"start": v(5, 35) * mm, "mid": v(3.75, 36.25) * mm, "end": v(2.5, 35) * mm});
            skArc(sketch, "E325", {"start": v(-12.5, 30) * mm, "mid": v(-10.28, 32.87) * mm, "end": v(-9.13, 36.3) * mm});
            skArc(sketch, "E326.MirrorCS", {"start": v(12.5, 30) * mm, "mid": v(10.28, 32.87) * mm, "end": v(9.13, 36.3) * mm});
            skLineSegment(sketch, "E327", {"start": v(-7.15, 38) * mm, "end": v(7.15, 38) * mm});
            skPoint(sketch, "E328.visualSharp", {"position": v(-9, 38) * mm});
            skArc(sketch, "E328.filletArc", {"start": v(-7.15, 38) * mm, "mid": v(-8.45, 37.52) * mm, "end": v(-9.13, 36.3) * mm});
            skPoint(sketch, "E329.visualSharp", {"position": v(9, 38) * mm});
            skArc(sketch, "E329.filletArc", {"start": v(9.13, 36.3) * mm, "mid": v(8.45, 37.52) * mm, "end": v(7.15, 38) * mm});
            skCircle(sketch, "E330.MirrorC", {"center": v(21, 21) * mm, "radius": 1.65 * mm});
            skSolve(sketch);
        }
        {
            var Q0;
            Q0=makeQuery(id+"F42.imprint","IMPRINT",FACE,{"disambiguationData":[TD([[makeQuery(id+"F42.imprint","IMPRINT",EDGE,{"derivedFrom":sQuery(id+"F42.wireOp",EDGE,"E303")}),-1.0]])]});
            extrude(context, id + "F43", {"entities" : qUnion([Q0]), "depth" : 1.5 * mm});
        }
        {
            var Q0;
            Q0=makeQuery(id+"F11.opExtrude","CAP_FACE",FACE,{"disambiguationData":[OSD([sQuery(id+"F10.wireOp",EDGE,"E185"),sQuery(id+"F10.wireOp",EDGE,"E186"),sQuery(id+"F10.wireOp",EDGE,"E188"),sQuery(id+"F10.wireOp",EDGE,"E189.filletArc"),sQuery(id+"F10.wireOp",EDGE,"E191.MirrorCS"),sQuery(id+"F10.wireOp",EDGE,"E193.MirrorCS"),sQuery(id+"F10.wireOp",EDGE,"E194.MirrorC"),sQuery(id+"F10.wireOp",EDGE,"E196.MirrorCS"),sQuery(id+"F10.wireOp",EDGE,"E198.MirrorCS"),sQuery(id+"F10.wireOp",EDGE,"E199.MirrorCS"),sQuery(id+"F10.wireOp",EDGE,"E200.MirrorCS"),sQuery(id+"F10.wireOp",EDGE,"E201.MirrorCS"),sQuery(id+"F10.wireOp",EDGE,"E202.MirrorCS"),sQuery(id+"F10.wireOp",EDGE,"E203.MirrorCS"),sQuery(id+"F10.wireOp",EDGE,"E204.MirrorCS"),sQuery(id+"F10.wireOp",EDGE,"E205.MirrorC"),sQuery(id+"F10.wireOp",EDGE,"E206.MirrorC"),sQuery(id+"F10.wireOp",EDGE,"E207.bottom"),sQuery(id+"F10.wireOp",EDGE,"E207.top"),sQuery(id+"F10.wireOp",EDGE,"E207.left"),sQuery(id+"F10.wireOp",EDGE,"E207.right"),sQuery(id+"F10.wireOp",EDGE,"E208.MirrorCS"),sQuery(id+"F10.wireOp",EDGE,"E209.MirrorCS"),sQuery(id+"F10.wireOp",EDGE,"E210.MirrorCS"),sQuery(id+"F10.wireOp",EDGE,"E211.MirrorCS"),sQuery(id+"F10.wireOp",EDGE,"E214"),sQuery(id+"F10.wireOp",EDGE,"E215"),sQuery(id+"F10.wireOp",EDGE,"E216.MirrorCS"),sQuery(id+"F10.wireOp",EDGE,"E217"),sQuery(id+"F10.wireOp",EDGE,"E218.trimOffspring"),sQuery(id+"F10.wireOp",EDGE,"E220.0.startCap"),sQuery(id+"F10.wireOp",EDGE,"E220.0.endCap"),sQuery(id+"F10.wireOp",EDGE,"E220.0.left"),sQuery(id+"F10.wireOp",EDGE,"E220.0.right"),sQuery(id+"F10.wireOp",EDGE,"E221.MirrorCS"),sQuery(id+"F10.wireOp",EDGE,"E222.MirrorCS"),sQuery(id+"F10.wireOp",EDGE,"E223.MirrorCS"),sQuery(id+"F10.wireOp",EDGE,"E224.MirrorCS"),sQuery(id+"F10.wireOp",EDGE,"E226"),sQuery(id+"F10.wireOp",EDGE,"E227"),sQuery(id+"F10.wireOp",EDGE,"E228"),sQuery(id+"F10.wireOp",EDGE,"E229"),sQuery(id+"F10.wireOp",EDGE,"E230.MirrorCS"),sQuery(id+"F10.wireOp",EDGE,"E231")])],"isStart":false});
            var sketch = newSketch(context, id + "F44", { "sketchPlane" : qUnion([Q0])});
            skLineSegment(sketch, "E331", {"start": v(-9.5, 12) * mm, "end": v(3.5, 12) * mm, "construction": true});
            skArc(sketch, "E332.0.startCap", {"start": v(-9.5, 10.75) * mm, "mid": v(-10.75, 12) * mm, "end": v(-9.5, 13.25) * mm});
            skArc(sketch, "E332.0.endCap", {"start": v(3.5, 13.25) * mm, "mid": v(4.75, 12) * mm, "end": v(3.5, 10.75) * mm});
            skLineSegment(sketch, "E332.0.left", {"start": v(-9.5, 13.25) * mm, "end": v(3.5, 13.25) * mm});
            skLineSegment(sketch, "E332.0.right", {"start": v(-9.5, 10.75) * mm, "end": v(3.5, 10.75) * mm});
            skLineSegment(sketch, "E333.0.1.0", {"start": v(-9.5, 6) * mm, "end": v(3.5, 6) * mm, "construction": true});
            skArc(sketch, "E333.0.1.1", {"start": v(-9.5, 4.75) * mm, "mid": v(-10.75, 6) * mm, "end": v(-9.5, 7.25) * mm});
            skLineSegment(sketch, "E333.0.1.2", {"start": v(-9.5, 4.75) * mm, "end": v(3.5, 4.75) * mm});
            skLineSegment(sketch, "E333.0.1.3", {"start": v(-9.5, 7.25) * mm, "end": v(3.5, 7.25) * mm});
            skArc(sketch, "E333.0.1.4", {"start": v(3.5, 7.25) * mm, "mid": v(4.75, 6) * mm, "end": v(3.5, 4.75) * mm});
            skLineSegment(sketch, "E333.0.2.0", {"start": v(-9.5, 0) * mm, "end": v(3.5, 0) * mm, "construction": true});
            skArc(sketch, "E333.0.2.1", {"start": v(-9.5, -1.25) * mm, "mid": v(-10.75, 0) * mm, "end": v(-9.5, 1.25) * mm});
            skLineSegment(sketch, "E333.0.2.2", {"start": v(-9.5, -1.25) * mm, "end": v(3.5, -1.25) * mm});
            skLineSegment(sketch, "E333.0.2.3", {"start": v(-9.5, 1.25) * mm, "end": v(3.5, 1.25) * mm});
            skArc(sketch, "E333.0.2.4", {"start": v(3.5, 1.25) * mm, "mid": v(4.75, 0) * mm, "end": v(3.5, -1.25) * mm});
            skLineSegment(sketch, "E333.0.3.0", {"start": v(-9.5, -6) * mm, "end": v(3.5, -6) * mm, "construction": true});
            skArc(sketch, "E333.0.3.1", {"start": v(-9.5, -7.25) * mm, "mid": v(-10.75, -6) * mm, "end": v(-9.5, -4.75) * mm});
            skLineSegment(sketch, "E333.0.3.2", {"start": v(-9.5, -7.25) * mm, "end": v(3.5, -7.25) * mm});
            skLineSegment(sketch, "E333.0.3.3", {"start": v(-9.5, -4.75) * mm, "end": v(3.5, -4.75) * mm});
            skArc(sketch, "E333.0.3.4", {"start": v(3.5, -4.75) * mm, "mid": v(4.75, -6) * mm, "end": v(3.5, -7.25) * mm});
            skLineSegment(sketch, "E333.0.4.0", {"start": v(-9.5, -12) * mm, "end": v(3.5, -12) * mm, "construction": true});
            skArc(sketch, "E333.0.4.1", {"start": v(-9.5, -13.25) * mm, "mid": v(-10.75, -12) * mm, "end": v(-9.5, -10.75) * mm});
            skLineSegment(sketch, "E333.0.4.2", {"start": v(-9.5, -13.25) * mm, "end": v(3.5, -13.25) * mm});
            skLineSegment(sketch, "E333.0.4.3", {"start": v(-9.5, -10.75) * mm, "end": v(3.5, -10.75) * mm});
            skArc(sketch, "E333.0.4.4", {"start": v(3.5, -10.75) * mm, "mid": v(4.75, -12) * mm, "end": v(3.5, -13.25) * mm});
            skLineSegment(sketch, "E333.0.5.0", {"start": v(-9.5, -18) * mm, "end": v(3.5, -18) * mm, "construction": true});
            skArc(sketch, "E333.0.5.1", {"start": v(-9.5, -19.25) * mm, "mid": v(-10.75, -18) * mm, "end": v(-9.5, -16.75) * mm});
            skLineSegment(sketch, "E333.0.5.2", {"start": v(-9.5, -19.25) * mm, "end": v(3.5, -19.25) * mm});
            skLineSegment(sketch, "E333.0.5.3", {"start": v(-9.5, -16.75) * mm, "end": v(3.5, -16.75) * mm});
            skArc(sketch, "E333.0.5.4", {"start": v(3.5, -16.75) * mm, "mid": v(4.75, -18) * mm, "end": v(3.5, -19.25) * mm});
            skLineSegment(sketch, "E333.direction1", {"start": v(-11.5, 8.75) * mm, "end": v(11.5, 8.75) * mm, "construction": true});
            skLineSegment(sketch, "E333.direction2", {"start": v(-11.5, 8.75) * mm, "end": v(-11.5, 2.75) * mm, "construction": true});
            skLineSegment(sketch, "E334", {"start": v(-16, 15.75) * mm, "end": v(-16, 2.75) * mm, "construction": true});
            skArc(sketch, "E335.0.startCap", {"start": v(-17.25, 15.75) * mm, "mid": v(-16, 17) * mm, "end": v(-14.75, 15.75) * mm});
            skArc(sketch, "E335.0.endCap", {"start": v(-14.75, 2.75) * mm, "mid": v(-16, 1.5) * mm, "end": v(-17.25, 2.75) * mm});
            skLineSegment(sketch, "E335.0.left", {"start": v(-14.75, 15.75) * mm, "end": v(-14.75, 2.75) * mm});
            skLineSegment(sketch, "E335.0.right", {"start": v(-17.25, 15.75) * mm, "end": v(-17.25, 2.75) * mm});
            skLineSegment(sketch, "E336.MirrorCS", {"start": v(-16, -15.75) * mm, "end": v(-16, -2.75) * mm, "construction": true});
            skLineSegment(sketch, "E337.MirrorCS", {"start": v(-14.75, -15.75) * mm, "end": v(-14.75, -2.75) * mm});
            skLineSegment(sketch, "E338.MirrorCS", {"start": v(-17.25, -15.75) * mm, "end": v(-17.25, -2.75) * mm});
            skArc(sketch, "E339.MirrorCS", {"start": v(-17.25, -15.75) * mm, "mid": v(-16, -17) * mm, "end": v(-14.75, -15.75) * mm});
            skArc(sketch, "E340.MirrorCS", {"start": v(-14.75, -2.75) * mm, "mid": v(-16, -1.5) * mm, "end": v(-17.25, -2.75) * mm});
            skLineSegment(sketch, "E341.MirrorCS", {"start": v(14.75, 15.75) * mm, "end": v(14.75, 2.75) * mm});
            skLineSegment(sketch, "E342.MirrorCS", {"start": v(17.25, -15.75) * mm, "end": v(17.25, -2.75) * mm});
            skArc(sketch, "E343.MirrorCS", {"start": v(14.75, 2.75) * mm, "mid": v(16, 1.5) * mm, "end": v(17.25, 2.75) * mm});
            skArc(sketch, "E344.MirrorCS", {"start": v(14.75, -2.75) * mm, "mid": v(16, -1.5) * mm, "end": v(17.25, -2.75) * mm});
            skLineSegment(sketch, "E345.MirrorCS", {"start": v(14.75, -15.75) * mm, "end": v(14.75, -2.75) * mm});
            skArc(sketch, "E346.MirrorCS", {"start": v(17.25, 15.75) * mm, "mid": v(16, 17) * mm, "end": v(14.75, 15.75) * mm});
            skLineSegment(sketch, "E347.MirrorCS", {"start": v(16, 15.75) * mm, "end": v(16, 2.75) * mm, "construction": true});
            skLineSegment(sketch, "E348.MirrorCS", {"start": v(17.25, 15.75) * mm, "end": v(17.25, 2.75) * mm});
            skLineSegment(sketch, "E349.MirrorCS", {"start": v(16, -15.75) * mm, "end": v(16, -2.75) * mm, "construction": true});
            skArc(sketch, "E350.MirrorCS", {"start": v(17.25, -15.75) * mm, "mid": v(16, -17) * mm, "end": v(14.75, -15.75) * mm});
            skLineSegment(sketch, "E351.0.0.6", {"start": v(-9.5, -24) * mm, "end": v(3.5, -24) * mm, "construction": true});
            skArc(sketch, "E351.3.0.6", {"start": v(-9.5, -25.25) * mm, "mid": v(-10.75, -24) * mm, "end": v(-9.5, -22.75) * mm});
            skLineSegment(sketch, "E351.7.0.6", {"start": v(-9.5, -25.25) * mm, "end": v(3.5, -25.25) * mm});
            skLineSegment(sketch, "E351.10.0.6", {"start": v(-9.5, -22.75) * mm, "end": v(3.5, -22.75) * mm});
            skArc(sketch, "E351.13.0.6", {"start": v(3.5, -22.75) * mm, "mid": v(4.75, -24) * mm, "end": v(3.5, -25.25) * mm});
            skSolve(sketch);
        }
        {
            var Q0;
            Q0=qSketchRegion(id+"F44",true);
            extrude(context, id + "F45", {"entities" : qUnion([Q0]), "operationType" : NewBodyOperationType.REMOVE, "oppositeDirection" : true, "depth" : 25 * mm});
        }
        {
            var Q0;
            Q0=makeQuery(id+"F3.opExtrude","CAP_FACE",FACE,{"disambiguationData":[OSD([sQuery(id+"F2.wireOp",EDGE,"E73"),sQuery(id+"F2.wireOp",EDGE,"E74"),sQuery(id+"F2.wireOp",EDGE,"E75"),sQuery(id+"F2.wireOp",EDGE,"E76"),sQuery(id+"F2.wireOp",EDGE,"E77.filletArc"),sQuery(id+"F2.wireOp",EDGE,"E79.MirrorCS"),sQuery(id+"F2.wireOp",EDGE,"E80.MirrorCS"),sQuery(id+"F2.wireOp",EDGE,"E81.MirrorCS"),sQuery(id+"F2.wireOp",EDGE,"E82.MirrorC"),sQuery(id+"F2.wireOp",EDGE,"E83.MirrorC"),sQuery(id+"F2.wireOp",EDGE,"E86.MirrorCS"),sQuery(id+"F2.wireOp",EDGE,"E87.MirrorCS"),sQuery(id+"F2.wireOp",EDGE,"E88.MirrorCS"),sQuery(id+"F2.wireOp",EDGE,"E89.MirrorCS"),sQuery(id+"F2.wireOp",EDGE,"E91.MirrorC"),sQuery(id+"F2.wireOp",EDGE,"E92.MirrorC"),sQuery(id+"F2.wireOp",EDGE,"E93.MirrorCS"),sQuery(id+"F2.wireOp",EDGE,"E94.MirrorC"),sQuery(id+"F2.wireOp",EDGE,"E95.MirrorC"),sQuery(id+"F2.wireOp",EDGE,"E96.MirrorCS"),sQuery(id+"F2.wireOp",EDGE,"E97.MirrorCS"),sQuery(id+"F2.wireOp",EDGE,"E98.MirrorCS"),sQuery(id+"F2.wireOp",EDGE,"E99.bottom"),sQuery(id+"F2.wireOp",EDGE,"E99.top"),sQuery(id+"F2.wireOp",EDGE,"E99.left"),sQuery(id+"F2.wireOp",EDGE,"E99.right"),sQuery(id+"F2.wireOp",EDGE,"E100.MirrorCS"),sQuery(id+"F2.wireOp",EDGE,"E101.MirrorCS"),sQuery(id+"F2.wireOp",EDGE,"E102.MirrorCS"),sQuery(id+"F2.wireOp",EDGE,"E103.MirrorCS"),sQuery(id+"F2.wireOp",EDGE,"E106"),sQuery(id+"F2.wireOp",EDGE,"E107"),sQuery(id+"F2.wireOp",EDGE,"E108.MirrorCS"),sQuery(id+"F2.wireOp",EDGE,"E109.MirrorCS"),sQuery(id+"F2.wireOp",EDGE,"E110.filletArc"),sQuery(id+"F2.wireOp",EDGE,"E111.filletArc"),sQuery(id+"F2.wireOp",EDGE,"E112"),sQuery(id+"F2.wireOp",EDGE,"E114.MirrorCS"),sQuery(id+"F2.wireOp",EDGE,"E115.MirrorCS"),sQuery(id+"F2.wireOp",EDGE,"E116.MirrorCS"),sQuery(id+"F2.wireOp",EDGE,"E119"),sQuery(id+"F2.wireOp",EDGE,"E120"),sQuery(id+"F2.wireOp",EDGE,"E121.MirrorCS"),sQuery(id+"F2.wireOp",EDGE,"E122.MirrorCS"),sQuery(id+"F2.wireOp",EDGE,"E123"),sQuery(id+"F2.wireOp",EDGE,"E124.MirrorCS"),sQuery(id+"F2.wireOp",EDGE,"E125.filletArc"),sQuery(id+"F2.wireOp",EDGE,"E126.filletArc"),sQuery(id+"F2.wireOp",EDGE,"E127"),sQuery(id+"F2.wireOp",EDGE,"E130.filletArc"),sQuery(id+"F2.wireOp",EDGE,"E131.filletArc")])],"isStart":false});
            var sketch = newSketch(context, id + "F46", { "sketchPlane" : qUnion([Q0])});
            skArc(sketch, "E352", {"start": v(-1.84, -41.02) * mm, "mid": v(-3.61, -37.2) * mm, "end": v(-5.6, -33.5) * mm});
            skArc(sketch, "E353.MirrorC", {"start": v(1.84, -41.02) * mm, "mid": v(3.61, -37.2) * mm, "end": v(5.6, -33.5) * mm});
            skLineSegment(sketch, "E354", {"start": v(-4.73, -32) * mm, "end": v(4.73, -32) * mm});
            skPoint(sketch, "E355.visualSharp", {"position": v(0, -45.71) * mm});
            skArc(sketch, "E355.filletArc", {"start": v(-1.84, -41.02) * mm, "mid": v(0, -42.23) * mm, "end": v(1.84, -41.02) * mm});
            skPoint(sketch, "E356.visualSharp", {"position": v(-6.47, -32) * mm});
            skArc(sketch, "E356.filletArc", {"start": v(-4.73, -32) * mm, "mid": v(-5.6, -32.5) * mm, "end": v(-5.6, -33.5) * mm});
            skPoint(sketch, "E357.visualSharp", {"position": v(6.47, -32) * mm});
            skArc(sketch, "E357.filletArc", {"start": v(5.6, -33.5) * mm, "mid": v(5.6, -32.5) * mm, "end": v(4.73, -32) * mm});
            skSolve(sketch);
        }
        {
            var Q0;
            Q0=qSketchRegion(id+"F46",true);
            extrude(context, id + "F47", {"entities" : qUnion([Q0]), "operationType" : NewBodyOperationType.REMOVE, "oppositeDirection" : true, "depth" : 25 * mm});
        }
        {
            var Q0;
            Q0=qCreatedBy(makeId("Top.planeOp"),FACE);
            var sketch = newSketch(context, id + "F48", { "sketchPlane" : qUnion([Q0])});
            skLineSegment(sketch, "E358", {"start": v(0, 0) * mm, "end": v(-70.71, 70.71) * mm, "construction": true});
            skLineSegment(sketch, "E359", {"start": v(-70.71, 70.71) * mm, "end": v(-70.71, 96.71) * mm, "construction": true});
            skCircle(sketch, "E360", {"center": v(-15.25, 15.25) * mm, "radius": 1.57 * mm});
            skCircle(sketch, "E361", {"center": v(-21, 21) * mm, "radius": 1.57 * mm});
            skArc(sketch, "E362", {"start": v(-26.85, 17.16) * mm, "mid": v(-26.43, 16.58) * mm, "end": v(-25.95, 16.05) * mm});
            skArc(sketch, "E363", {"start": v(-85.64, 98.17) * mm, "mid": v(-83.77, 89.33) * mm, "end": v(-77.15, 83.16) * mm});
            skCircle(sketch, "E364", {"center": v(-70.71, 96.71) * mm, "radius": 4 * mm});
            skLineSegment(sketch, "E365", {"start": v(0, 0) * mm, "end": v(-70.71, 96.71) * mm, "construction": true});
            skLineSegment(sketch, "E366", {"start": v(-70.71, 96.71) * mm, "end": v(-79.5, 110.09) * mm, "construction": true});
            skArc(sketch, "E367", {"start": v(-75.33, 115.72) * mm, "mid": v(-83.33, 115.94) * mm, "end": v(-86.31, 108.5) * mm});
            skCircle(sketch, "E368", {"center": v(-79.5, 110.09) * mm, "radius": 3 * mm});
            skPoint(sketch, "E369.visualSharp", {"position": v(-83.59, 104.4) * mm});
            skArc(sketch, "E369.filletArc", {"start": v(-85.64, 98.17) * mm, "mid": v(-85.55, 103.37) * mm, "end": v(-86.31, 108.5) * mm});
            skPoint(sketch, "E370.visualSharp", {"position": v(-72.65, 111.58) * mm});
            skArc(sketch, "E370.filletArc", {"start": v(-75.33, 115.72) * mm, "mid": v(-70.92, 112.98) * mm, "end": v(-66.12, 110.99) * mm});
            skLineSegment(sketch, "E371", {"start": v(-49.18, 76.67) * mm, "end": v(-16.1, 26.3) * mm});
            skLineSegment(sketch, "E372", {"start": v(-60.88, 69) * mm, "end": v(-26.85, 17.16) * mm});
            skLineSegment(sketch, "E373", {"start": v(-70.71, 96.71) * mm, "end": v(-21, 21) * mm, "construction": true});
            skArc(sketch, "E374.trimOffspring", {"start": v(-55.72, 97.23) * mm, "mid": v(-58.74, 105.76) * mm, "end": v(-66.12, 110.99) * mm});
            skLineSegment(sketch, "E375", {"start": v(-25.95, 16.05) * mm, "end": v(-9.9, 0) * mm});
            skLineSegment(sketch, "E376", {"start": v(-9.9, 0) * mm, "end": v(0, 0) * mm});
            skLineSegment(sketch, "E377", {"start": v(0, 0) * mm, "end": v(0, 9.9) * mm});
            skLineSegment(sketch, "E378", {"start": v(0, 9.9) * mm, "end": v(-14.82, 24.72) * mm});
            skPoint(sketch, "E379.visualSharp", {"position": v(-15.54, 25.44) * mm});
            skArc(sketch, "E379.filletArc", {"start": v(-16.1, 26.3) * mm, "mid": v(-15.5, 25.48) * mm, "end": v(-14.82, 24.72) * mm});
            skPoint(sketch, "E380.visualSharp", {"position": v(-69.28, 81.78) * mm});
            skArc(sketch, "E380.filletArc", {"start": v(-60.88, 69) * mm, "mid": v(-68.04, 77.2) * mm, "end": v(-77.15, 83.16) * mm});
            skPoint(sketch, "E381.visualSharp", {"position": v(-57.58, 89.46) * mm});
            skArc(sketch, "E381.filletArc", {"start": v(-55.72, 97.23) * mm, "mid": v(-53.86, 86.5) * mm, "end": v(-49.18, 76.67) * mm});
            skSolve(sketch);
        }
        {
            var Q0;
            Q0=makeQuery(id+"F48.imprint","IMPRINT",FACE,{"disambiguationData":[TD([[makeQuery(id+"F48.imprint","IMPRINT",EDGE,{"derivedFrom":sQuery(id+"F48.wireOp",EDGE,"E360")}),-1.0]])]});
            extrude(context, id + "F49", {"entities" : qUnion([Q0]), "depth" : 4 * mm, "offsetDistance" : 25 * mm});
        }
        {
            var Q0;
            Q0=makeQuery(id+"F49.opExtrude","CAP_FACE",FACE,{"disambiguationData":[OSD([sQuery(id+"F48.wireOp",EDGE,"E360"),sQuery(id+"F48.wireOp",EDGE,"E361"),sQuery(id+"F48.wireOp",EDGE,"E362"),sQuery(id+"F48.wireOp",EDGE,"E363"),sQuery(id+"F48.wireOp",EDGE,"E364"),sQuery(id+"F48.wireOp",EDGE,"E367"),sQuery(id+"F48.wireOp",EDGE,"E368"),sQuery(id+"F48.wireOp",EDGE,"E369.filletArc"),sQuery(id+"F48.wireOp",EDGE,"E370.filletArc"),sQuery(id+"F48.wireOp",EDGE,"E371"),sQuery(id+"F48.wireOp",EDGE,"E372"),sQuery(id+"F48.wireOp",EDGE,"E374.trimOffspring"),sQuery(id+"F48.wireOp",EDGE,"E375"),sQuery(id+"F48.wireOp",EDGE,"E376"),sQuery(id+"F48.wireOp",EDGE,"E377"),sQuery(id+"F48.wireOp",EDGE,"E378"),sQuery(id+"F48.wireOp",EDGE,"E379.filletArc"),sQuery(id+"F48.wireOp",EDGE,"E380.filletArc"),sQuery(id+"F48.wireOp",EDGE,"E381.filletArc")])],"isStart":false});
            var sketch = newSketch(context, id + "F50", { "sketchPlane" : qUnion([Q0])});
            skCircle(sketch, "E382", {"center": v(-70.71, 96.71) * mm, "radius": 7.75 * mm, "construction": true});
            skCircle(sketch, "E383", {"center": v(-70.71, 96.71) * mm, "radius": 9.5 * mm, "construction": true});
            skLineSegment(sketch, "E384", {"start": v(-70.71, 96.71) * mm, "end": v(-69.14, 104.3) * mm, "construction": true});
            skLineSegment(sketch, "E385", {"start": v(-70.71, 96.71) * mm, "end": v(-21, 21) * mm, "construction": true});
            skLineSegment(sketch, "E386", {"start": v(-69.14, 104.3) * mm, "end": v(-68.78, 106.01) * mm, "construction": true});
            skArc(sketch, "E387.0.startCap", {"start": v(-67.6, 103.98) * mm, "mid": v(-69.46, 102.76) * mm, "end": v(-70.68, 104.62) * mm});
            skArc(sketch, "E387.0.endCap", {"start": v(-70.32, 106.33) * mm, "mid": v(-68.46, 107.56) * mm, "end": v(-67.24, 105.7) * mm});
            skLineSegment(sketch, "E387.0.left", {"start": v(-70.68, 104.62) * mm, "end": v(-70.32, 106.33) * mm});
            skLineSegment(sketch, "E387.0.right", {"start": v(-67.6, 103.98) * mm, "end": v(-67.24, 105.7) * mm});
            skArc(sketch, "E388.1.0", {"start": v(-80.33, 97.1) * mm, "mid": v(-81.56, 98.96) * mm, "end": v(-79.7, 100.18) * mm});
            skArc(sketch, "E388.1.1", {"start": v(-77.98, 99.83) * mm, "mid": v(-76.76, 97.96) * mm, "end": v(-78.62, 96.74) * mm});
            skLineSegment(sketch, "E388.1.2", {"start": v(-78.3, 98.28) * mm, "end": v(-80.01, 98.64) * mm, "construction": true});
            skLineSegment(sketch, "E388.1.3", {"start": v(-77.98, 99.83) * mm, "end": v(-79.7, 100.18) * mm});
            skLineSegment(sketch, "E388.1.4", {"start": v(-78.62, 96.74) * mm, "end": v(-80.33, 97.1) * mm});
            skArc(sketch, "E388.2.0", {"start": v(-71.1, 87.09) * mm, "mid": v(-72.96, 85.87) * mm, "end": v(-74.18, 87.73) * mm});
            skArc(sketch, "E388.2.1", {"start": v(-73.83, 89.44) * mm, "mid": v(-71.96, 90.66) * mm, "end": v(-70.74, 88.8) * mm});
            skLineSegment(sketch, "E388.2.2", {"start": v(-72.28, 89.12) * mm, "end": v(-72.64, 87.4) * mm, "construction": true});
            skLineSegment(sketch, "E388.2.3", {"start": v(-73.83, 89.44) * mm, "end": v(-74.18, 87.73) * mm});
            skLineSegment(sketch, "E388.2.4", {"start": v(-70.74, 88.8) * mm, "end": v(-71.1, 87.09) * mm});
            skArc(sketch, "E388.3.0", {"start": v(-61.09, 96.32) * mm, "mid": v(-59.87, 94.46) * mm, "end": v(-61.73, 93.24) * mm});
            skArc(sketch, "E388.3.1", {"start": v(-63.44, 93.6) * mm, "mid": v(-64.66, 95.46) * mm, "end": v(-62.8, 96.68) * mm});
            skLineSegment(sketch, "E388.3.2", {"start": v(-63.12, 95.14) * mm, "end": v(-61.4, 94.78) * mm, "construction": true});
            skLineSegment(sketch, "E388.3.3", {"start": v(-63.44, 93.6) * mm, "end": v(-61.73, 93.24) * mm});
            skLineSegment(sketch, "E388.3.4", {"start": v(-62.8, 96.68) * mm, "end": v(-61.09, 96.32) * mm});
            skSolve(sketch);
        }
        {
            var Q0;
            Q0=qSketchRegion(id+"F50",true);
            extrude(context, id + "F51", {"entities" : qUnion([Q0]), "operationType" : NewBodyOperationType.REMOVE, "oppositeDirection" : true, "depth" : 25 * mm, "offsetDistance" : 25 * mm});
        }
        {
            var Q0;
            Q0=makeQuery(id+"F7.opExtrude","SWEPT_EDGE",EDGE,{"disambiguationData":[OSD([sQuery(id+"F6.wireOp",EDGE,"E145"),sQuery(id+"F6.wireOp",EDGE,"E178.MirrorCS")])]});
            var Q1;
            Q1=makeQuery(id+"F7.opExtrude","SWEPT_EDGE",EDGE,{"disambiguationData":[OSD([sQuery(id+"F6.wireOp",EDGE,"E178.MirrorCS"),sQuery(id+"F6.wireOp",EDGE,"E179.trimOffspring")])]});
            var Q2;
            Q2=makeQuery(id+"F7.opExtrude","SWEPT_EDGE",EDGE,{"disambiguationData":[OSD([sQuery(id+"F6.wireOp",EDGE,"E175"),sQuery(id+"F6.wireOp",EDGE,"E176.trimOffspring")])]});
            var Q3;
            Q3=makeQuery(id+"F7.opExtrude","SWEPT_EDGE",EDGE,{"disambiguationData":[OSD([sQuery(id+"F6.wireOp",EDGE,"E152.trimOffspring"),sQuery(id+"F6.wireOp",EDGE,"E175")])]});
            fillet(context, id + "F52", {"entities" : qUnion([Q0, Q1, Q2, Q3]), "radius" : 5 * mm, "tangentPropagation" : true, "allowEdgeOverflow" : false});
        }
        {
            var Q0;
            Q0=makeQuery(id+"F7.opExtrude","SWEPT_EDGE",EDGE,{"disambiguationData":[OSD([sQuery(id+"F6.wireOp",EDGE,"E157"),sQuery(id+"F6.wireOp",EDGE,"E166")])]});
            fillet(context, id + "F53", {"entities" : qUnion([Q0]), "radius" : 1 * mm, "tangentPropagation" : true, "allowEdgeOverflow" : false});
        }
        {
            var Q0;
            Q0=makeQuery(id+"F0.imprint","IMPRINT",FACE,{"disambiguationData":[TD([[makeQuery(id+"F0.imprint","IMPRINT",EDGE,{"derivedFrom":sQuery(id+"F0.wireOp",EDGE,"E0")}),-1.0]])]});
            extrude(context, id + "F54", {"entities" : qUnion([Q0]), "depth" : 1.5 * mm, "offsetDistance" : 25 * mm});
        }
        {
            var Q0;
            Q0=makeQuery(id+"F54.opExtrude","SWEPT_EDGE",EDGE,{"disambiguationData":[OSD([sQuery(id+"F0.wireOp",EDGE,"E17.MirrorCS"),sQuery(id+"F0.wireOp",EDGE,"E40.MirrorCS")])]});
            var Q1;
            Q1=makeQuery(id+"F54.opExtrude","SWEPT_EDGE",EDGE,{"disambiguationData":[OSD([sQuery(id+"F0.wireOp",EDGE,"E18.MirrorCS"),sQuery(id+"F0.wireOp",EDGE,"E40.MirrorCS")])]});
            var Q2;
            Q2=makeQuery(id+"F54.opExtrude","SWEPT_EDGE",EDGE,{"disambiguationData":[OSD([sQuery(id+"F0.wireOp",EDGE,"E12.MirrorCS"),sQuery(id+"F0.wireOp",EDGE,"E26")])]});
            var Q3;
            Q3=makeQuery(id+"F54.opExtrude","SWEPT_EDGE",EDGE,{"disambiguationData":[OSD([sQuery(id+"F0.wireOp",EDGE,"E11"),sQuery(id+"F0.wireOp",EDGE,"E26")])]});
            fillet(context, id + "F55", {"entities" : qUnion([Q0, Q1, Q2, Q3]), "radius" : 6.66 * mm, "tangentPropagation" : true, "allowEdgeOverflow" : false});
        }
    });
